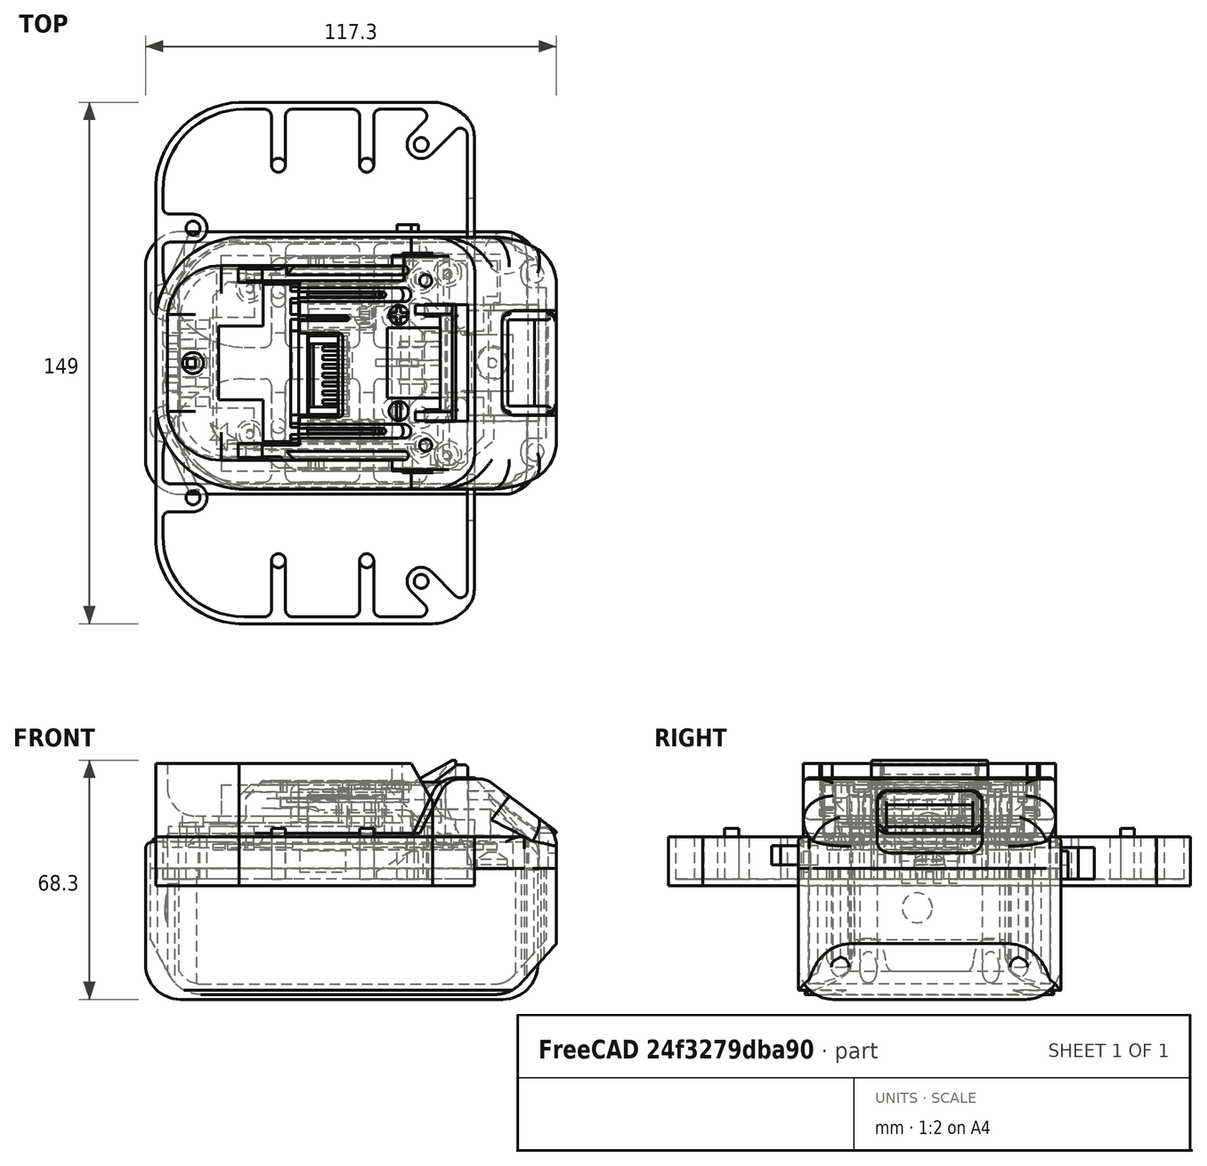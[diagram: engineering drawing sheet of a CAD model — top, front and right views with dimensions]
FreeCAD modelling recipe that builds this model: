
FCSTD DOCUMENT  (FreeCAD 1.0R39319 (Git))
Label: Makita LXT 18V - Battery Adapter v3
License: Creative Commons Attribution 4.0
LicenseURL: https://creativecommons.org/licenses/by/4.0/
objects: Sketcher::SketchObject×28, TechDraw::DrawViewDimension×26, PartDesign::Pocket×18, Part::Feature×12, Image::ImagePlane×8, PartDesign::Pad×6, App::Part×4, PartDesign::Body×4, TechDraw::DrawProjGroupItem×4, PartDesign::Mirrored×3, Mesh::Feature×2, PartDesign::ShapeBinder×2, TechDraw::DrawSVGTemplate×2, TechDraw::DrawPage×2, App::DocumentObjectGroup×1, PartDesign::Fillet×1
note: 204 computed .brp shape members not serialized (recipe doc carries the construction recipe); baked Part::Feature solids carry a one-line shape summary decoded from their .brp

FEATURE [Image::ImagePlane] _d371b5c4eb3955924449baf6266c6d76947dcc9_original  label="7d371b5c4eb3955924449baf6266c6d76947dcc9_original"
  Placement = pos=(41.6,-9,0) rot=(0,0,1;3.14159rad)
  XSize = 126.335
  YSize = 126.335
FEATURE [Part::Feature] Part__Feature  label="Battery Plate"
  shape: bbox 116 x 75.01 x 30.55 mm, 339 faces (baked)
FEATURE [Part::Feature] Part__Feature001  label="Battery Clip"
  shape: bbox 37.48 x 33.31 x 30.03 mm, 74 faces (baked)
FEATURE [Part::Feature] Part__Feature002  label="Yellow Connector"
  shape: bbox 11 x 22.5 x 15.5 mm, 45 faces (baked)
FEATURE [Part::Feature] Part__Feature003  label="Power Clips"
  shape: bbox 20 x 5.5 x 13.5 mm, 10 faces (baked)
FEATURE [Part::Feature] Part__Feature004  label="Power Clips001"
  shape: bbox 18 x 5.5 x 13.5 mm, 10 faces (baked)
FEATURE [Part::Feature] Part__Feature005  label="Power Clips002"
  shape: bbox 20 x 5.5 x 13.5 mm, 10 faces (baked)
FEATURE [App::Part] Power_Clips  label="Power Clips003"
  Group = -> [Part__Feature003,Part__Feature004,Part__Feature005]
  Origin = -> Origin
FEATURE [Part::Feature] Part__Feature006  label="SOLID"
  shape: bbox 81.05 x 58.5 x 1.6 mm, 23 faces (baked)
FEATURE [App::Part] BMS
  Group = -> [Part__Feature002,Power_Clips,Part__Feature006]
  Origin = -> Origin001
FEATURE [Part::Feature] Part__Feature007  label="Case"
  shape: bbox 116 x 75 x 36 mm, 85 faces (baked)
FEATURE [Part::Feature] Part__Feature008  label="Case001"
  shape: bbox 0.6 x 8.5 x 8.5 mm, 3 faces (baked)
FEATURE [App::Part] Case  label="Case002"
  Group = -> [Part__Feature007,Part__Feature008]
  Origin = -> Origin002
FEATURE [App::Part] Battery_LxT_18V_v7  label="Battery LxT 18V v7"
  Group = -> [Part__Feature,Part__Feature001,BMS,Case]
  Origin = -> Origin003
  Placement = pos=(-3.4,0,-1.2) rot=(0,0,1;0rad)
FEATURE [Image::ImagePlane] Makita_Adapter_BL14xx_BL18xx_Zeichnung_v13  label="Makita Adapter BL14xx BL18xx Zeichnung v13"
  Placement = pos=(112.3,-1.5,0) rot=(0,0,1;0rad)
  XSize = 356.175
  YSize = 251.8
FEATURE [Mesh::Feature] Makita18V_BL1860B  label="Makita18V_BL1860B-1.1"
  Placement = pos=(49.6,-1.32e-14,-46.3) rot=(0,0,1;1.5708rad)
FEATURE [Part::Feature] Part__Feature009  label="Makita18V_BL1860B-2.1"
  Placement = pos=(49.7,-1.1e-14,-46.4) rot=(0,0,1;1.5708rad)
  shape: bbox 113.6 x 76.65 x 68.3 mm, 194 faces (baked)
FEATURE [Image::ImagePlane] ScreenShot2021_11_09at3  label="ScreenShot2021-11-09at3"
  Placement = pos=(105.7,-10.5,0) rot=(0,0,1;4.71239rad)
  XSize = 291.833
  YSize = 230.478
FEATURE [Image::ImagePlane] makita_battery_holder_mount  label="makita-battery-holder-mount"
  Placement = pos=(25.3,-0.5,0) rot=(0,0,1;4.71239rad)
  XSize = 296.506
  YSize = 208.851
FEATURE [Sketcher::SketchObject] Sketch  label="Top View"
  ArcFitTolerance = 1e-06
  AttachmentSupport = -> [XY_Plane004]
  FullyConstrained = true
  MakeInternals = false
  MapMode = 5
  sketch-geometry (13):
    g0: ArcOfCircle CenterX=14.9923 CenterY=12.0315 CenterZ=0 NormalX=0 NormalY=0 NormalZ=1 AngleXU=0 Radius=15 StartAngle=1.76483 EndAngle=3.1737
    g1: LineSegment StartX=0 StartY=0 StartZ=0 EndX=0 EndY=11.55 EndZ=0
    g2: LineSegment StartX=12.1 StartY=26.75 StartZ=0 EndX=66.6 EndY=26.75 EndZ=0
    g3: LineSegment StartX=-3.35 StartY=0 StartZ=0 EndX=-3.35 EndY=13 EndZ=0
    g4: LineSegment StartX=-3.35 StartY=0 StartZ=0 EndX=0 EndY=0 EndZ=0
    g5: LineSegment StartX=68.55 StartY=36 StartZ=0 EndX=20.45 EndY=36 EndZ=0
    g6: ArcOfCircle CenterX=21.7106 CenterY=10.8816 CenterZ=0 NormalX=0 NormalY=0 NormalZ=1 AngleXU=0 Radius=25.15 StartAngle=1.62094 EndAngle=3.05726
    g7: LineSegment StartX=87.55 StartY=0 StartZ=0 EndX=87.55 EndY=26.1 EndZ=0
    g8: LineSegment StartX=68.55 StartY=36 StartZ=0 EndX=75.7 EndY=36 EndZ=0
    g9: ArcOfCircle CenterX=79.8506 CenterY=26.1949 CenterZ=0 NormalX=0 NormalY=0 NormalZ=1 AngleXU=0 Radius=7.7 StartAngle=6.27086 EndAngle=6.98074
    g10: ArcOfCircle CenterX=75.3287 CenterY=22.4051 CenterZ=0 NormalX=0 NormalY=0 NormalZ=1 AngleXU=0 Radius=13.6 StartAngle=0.697551 EndAngle=1.54349
    g11: ArcOfCircle CenterX=7.275 CenterY=0 CenterZ=0 NormalX=0 NormalY=0 NormalZ=1 AngleXU=0 Radius=2 StartAngle=0 EndAngle=3.14159
    g12: Circle CenterX=72.4 CenterY=23.9 CenterZ=0 NormalX=0 NormalY=0 NormalZ=1 AngleXU=0 Radius=2
  constraints (44):
    c: PointOnObject(g0,g-2)
    c: Coincident(g1,g-1)
    c: Horizontal(g2)
    c: DistanceY(g1,g1) = 11.55
    c: DistanceY(g0) = 26.75
    c: Coincident(g2,g0)
    c: Coincident(g0,g1)
    c: Radius(g0) = 15
    c: DistanceX(g0) = 12.1
    c: DistanceX(g2) = 66.6
    c: PointOnObject(g3,g-1)
    c: Vertical(g3)
    c: Coincident(g4,g3)
    c: Coincident(g4,g1)
    c: Horizontal(g5)
    c: Coincident(g6,g3)
    c: Coincident(g6,g5)
    c: DistanceX(g3,g-1) = 3.35
    c: DistanceY(g3,g3) = 13
    c: DistanceY(g5) = 36
    c: DistanceX(g5) = 20.45
    c: Radius(g6) = 25.15
    c: DistanceX(g5) = 68.55
    c: PointOnObject(g7,g-1)
    c: Vertical(g7)
    c: DistanceX(g7) = 87.55
    c: DistanceY(g7,g7) = 26.1
    c: Coincident(g8,g5)
    c: Horizontal(g8)
    c: DistanceX(g8,g8) = 7.15
    c: Coincident(g9,g7)
    c: Coincident(g10,g8)
    c: Tangent(g10,g9) = -1.5708
    c: Radius(g10) = 13.6
    c: Radius(g9) = 7.7
    c: DistanceX(g9) = 85.752
    c: PointOnObject(g11,g-1)
    c: PointOnObject(g11,g-1)
    c: Equal(g12,g11)
    c: Diameter(g12) = 4
    c: DistanceX(g11,g7) = 80.275
    c: PointOnObject(g11,g-1)
    c: DistanceX(g12,g7) = 15.15
    c: DistanceY(g12) = 23.9
FEATURE [Part::Feature] Makita18V_BL1860B001  label="Makita18V_BL1860B-2.2"
  shape: bbox 112 x 75 x 68.3 mm, 4064 faces, 0 solids (baked)
FEATURE [Part::Feature] Makita18V_BL1860B002  label="Makita18V_BL1860B-1.2"
  shape: bbox 112 x 75 x 68.3 mm, 4064 faces, 0 solids (baked)
FEATURE [Sketcher::SketchObject] Sketch001  label="Top View001"
  ArcFitTolerance = 1e-06
  AttachmentSupport = -> [XY_Plane005]
  FullyConstrained = true
  MakeInternals = false
  MapMode = 5
  sketch-geometry (11):
    g0: ArcOfCircle CenterX=14.9923 CenterY=12.0315 CenterZ=0 NormalX=0 NormalY=0 NormalZ=1 AngleXU=0 Radius=15 StartAngle=1.76483 EndAngle=3.1737
    g1: LineSegment StartX=0 StartY=0 StartZ=0 EndX=0 EndY=11.55 EndZ=0
    g2: LineSegment StartX=12.1 StartY=26.75 StartZ=0 EndX=66.6 EndY=26.75 EndZ=0
    g3: LineSegment StartX=-3.35 StartY=0 StartZ=0 EndX=-3.35 EndY=13 EndZ=0
    g4: LineSegment StartX=-3.35 StartY=0 StartZ=0 EndX=0 EndY=0 EndZ=0
    g5: LineSegment StartX=68.55 StartY=36 StartZ=0 EndX=20.45 EndY=36 EndZ=0
    g6: ArcOfCircle CenterX=21.7106 CenterY=10.8816 CenterZ=0 NormalX=0 NormalY=0 NormalZ=1 AngleXU=0 Radius=25.15 StartAngle=1.62094 EndAngle=3.05726
    g7: LineSegment StartX=87.55 StartY=0 StartZ=0 EndX=87.55 EndY=26.1 EndZ=0
    g8: LineSegment StartX=68.55 StartY=36 StartZ=0 EndX=75.7 EndY=36 EndZ=0
    g9: ArcOfCircle CenterX=79.8506 CenterY=26.1949 CenterZ=0 NormalX=0 NormalY=0 NormalZ=1 AngleXU=0 Radius=7.7 StartAngle=6.27086 EndAngle=6.98074
    g10: ArcOfCircle CenterX=75.3287 CenterY=22.4051 CenterZ=0 NormalX=0 NormalY=0 NormalZ=1 AngleXU=0 Radius=13.6 StartAngle=0.697551 EndAngle=1.54349
  constraints (36):
    c: PointOnObject(g0,g-2)
    c: Coincident(g1,g-1)
    c: Horizontal(g2)
    c: DistanceY(g1,g1) = 11.55
    c: DistanceY(g0) = 26.75
    c: Coincident(g2,g0)
    c: Coincident(g0,g1)
    c: Radius(g0) = 15
    c: DistanceX(g0) = 12.1
    c: DistanceX(g2) = 66.6
    c: PointOnObject(g3,g-1)
    c: Vertical(g3)
    c: Coincident(g4,g3)
    c: Coincident(g4,g1)
    c: Horizontal(g5)
    c: Coincident(g6,g3)
    c: Coincident(g6,g5)
    c: DistanceX(g3,g-1) = 3.35
    c: DistanceY(g3,g3) = 13
    c: DistanceY(g5) = 36
    c: DistanceX(g5) = 20.45
    c: Radius(g6) = 25.15
    c: DistanceX(g5) = 68.55
    c: PointOnObject(g7,g-1)
    c: Vertical(g7)
    c: DistanceX(g7) = 87.55
    c: DistanceY(g7,g7) = 26.1
    c: Coincident(g8,g5)
    c: Horizontal(g8)
    c: DistanceX(g8,g8) = 7.15
    c: Coincident(g9,g7)
    c: Coincident(g10,g8)
    c: Tangent(g10,g9) = -1.5708
    c: Radius(g10) = 13.6
    c: Radius(g9) = 7.7
    c: DistanceX(g9) = 85.752
FEATURE [Sketcher::SketchObject] Sketch002
  ArcFitTolerance = 1e-06
  AttachmentSupport = -> [XY_Plane005]
  ExternalGeometry = -> [Sketch001]
  FullyConstrained = true
  MakeInternals = false
  MapMode = 5
  sketch-geometry (7):
    g0: LineSegment StartX=87.55 StartY=0 StartZ=0 EndX=87.55 EndY=26.1 EndZ=0
    g1: LineSegment StartX=87.55 StartY=0 StartZ=0 EndX=-3.35 EndY=0 EndZ=0
    g2: LineSegment StartX=-3.35 StartY=0 StartZ=0 EndX=-3.35 EndY=13 EndZ=0
    g3: LineSegment StartX=20.45 StartY=36 StartZ=0 EndX=75.7 EndY=36 EndZ=0
    g4: ArcOfCircle CenterX=21.7106 CenterY=10.8816 CenterZ=0 NormalX=0 NormalY=0 NormalZ=1 AngleXU=0 Radius=25.15 StartAngle=1.62094 EndAngle=3.05726
    g5: ArcOfCircle CenterX=79.8506 CenterY=26.1949 CenterZ=0 NormalX=0 NormalY=0 NormalZ=1 AngleXU=0 Radius=7.7 StartAngle=6.27086 EndAngle=6.98074
    g6: ArcOfCircle CenterX=75.3287 CenterY=22.4051 CenterZ=0 NormalX=0 NormalY=0 NormalZ=1 AngleXU=0 Radius=13.6 StartAngle=0.697551 EndAngle=1.54349
  constraints (19):
    c: PointOnObject(g0,g-1)
    c: Coincident(g0,g-3)
    c: Vertical(g0)
    c: Coincident(g1,g0)
    c: PointOnObject(g1,g-1)
    c: Coincident(g2,g1)
    c: Coincident(g2,g-5)
    c: Vertical(g2)
    c: Coincident(g3,g-5)
    c: Coincident(g3,g-4)
    c: Coincident(g4,g2)
    c: Coincident(g4,g3)
    c: Tangent(g4,g-5)
    c: Coincident(g5,g-4)
    c: Coincident(g5,g0)
    c: Tangent(g5,g-3)
    c: Coincident(g6,g5)
    c: Coincident(g6,g3)
    c: Tangent(g6,g-4)
FEATURE [Sketcher::SketchObject] Sketch003  label="Side View"
  ArcFitTolerance = 1e-06
  AttachmentSupport = -> [XZ_Plane004]
  ExternalGeometry = -> [Sketch]
  FullyConstrained = true
  MakeInternals = false
  MapMode = 5
  Placement = pos=(0,0,0) rot=(1,0,0;1.5708rad)
  sketch-geometry (8):
    g0: LineSegment StartX=69.6 StartY=0 StartZ=0 EndX=75.7032 EndY=13 EndZ=0
    g1: LineSegment StartX=87.55 StartY=17 StartZ=0 EndX=82 EndY=17 EndZ=0
    g2: ArcOfCircle CenterX=82 CenterY=10.0438 CenterZ=0 NormalX=0 NormalY=0 NormalZ=1 AngleXU=0 Radius=6.9562 StartAngle=1.5708 EndAngle=2.70266
    g3: LineSegment StartX=82.15 StartY=17 StartZ=0 EndX=82.15 EndY=22 EndZ=0
    g4: LineSegment StartX=82.15 StartY=22 StartZ=0 EndX=81.15 EndY=22 EndZ=0
    g5: LineSegment StartX=81.15 StartY=22 StartZ=0 EndX=70.65 EndY=16 EndZ=0
    g6: LineSegment StartX=70.65 StartY=16 StartZ=0 EndX=70.65 EndY=15 EndZ=0
    g7: LineSegment StartX=70.65 StartY=15 StartZ=0 EndX=77.1189 EndY=15 EndZ=0
  constraints (26):
    c: PointOnObject(g0,g-1)
    c: Horizontal(g1)
    c: Vertical(g1,g-3)
    c: DistanceX(g0) = 69.6
    c: DistanceY(g0) = 13
    c: DistanceY(g1) = 17
    c: DistanceX(g1) = 82
    c: Tangent(g2,g1) = -1.5708
    c: Tangent(g2,g0) = 1.5708
    c: Radius(g2) = 6.9562
    c: PointOnObject(g3,g1)
    c: Vertical(g3)
    c: Coincident(g3,g4)
    c: Horizontal(g4)
    c: Coincident(g4,g5)
    c: Coincident(g5,g6)
    c: Coincident(g6,g7)
    c: PointOnObject(g7,g2)
    c: Horizontal(g7)
    c: Vertical(g6)
    c: DistanceY(g6) = 15
    c: DistanceX(g6) = 70.65
    c: DistanceY(g6,g6) = 1
    c: DistanceY(g4) = 22
    c: DistanceX(g4) = 81.15
    c: DistanceX(g4,g4) = 1
FEATURE [PartDesign::Body] Body  label="Base Shape"
  AllowCompound = false
  Group = -> [Sketch,Sketch003]
  Origin = -> Origin004
FEATURE [PartDesign::Pad] Pad  label="Shell"
  Direction = (0,0,1)
  Length = 21
  Length2 = 10
  Profile = -> Sketch002
  ReferenceAxis = -> Sketch002 [N_Axis]
  Refine = true
  Suppressed = false
  Type = 0
FEATURE [Sketcher::SketchObject] Sketch004  label="Side View001"
  ArcFitTolerance = 1e-06
  AttachmentSupport = -> [XZ_Plane005]
  ExternalGeometry = -> [Sketch]
  FullyConstrained = true
  MakeInternals = false
  MapMode = 5
  Placement = pos=(0,0,0) rot=(1,0,0;1.5708rad)
  sketch-geometry (8):
    g0: LineSegment StartX=69.6 StartY=0 StartZ=0 EndX=76.8812 EndY=13 EndZ=0
    g1: LineSegment StartX=87.55 StartY=16 StartZ=0 EndX=82 EndY=16 EndZ=0
    g2: ArcOfCircle CenterX=82 CenterY=10.133 CenterZ=0 NormalX=0 NormalY=0 NormalZ=1 AngleXU=0 Radius=5.867 StartAngle=1.5708 EndAngle=2.63103
    g3: LineSegment StartX=82.15 StartY=16 StartZ=0 EndX=82.15 EndY=22 EndZ=0
    g4: LineSegment StartX=82.15 StartY=22 StartZ=0 EndX=81.15 EndY=22 EndZ=0
    g5: LineSegment StartX=81.15 StartY=22 StartZ=0 EndX=70.65 EndY=16 EndZ=0
    g6: LineSegment StartX=70.65 StartY=16 StartZ=0 EndX=70.65 EndY=15 EndZ=0
    g7: LineSegment StartX=70.65 StartY=15 StartZ=0 EndX=78.7237 EndY=15 EndZ=0
  constraints (26):
    c: PointOnObject(g0,g-1)
    c: Horizontal(g1)
    c: Vertical(g1,g-3)
    c: DistanceX(g0) = 69.6
    c: DistanceY(g0) = 13
    c: DistanceY(g1) = 16
    c: DistanceX(g1) = 82
    c: Tangent(g2,g1) = -1.5708
    c: Tangent(g2,g0) = 1.5708
    c: Radius(g2) = 5.867
    c: PointOnObject(g3,g1)
    c: Vertical(g3)
    c: Coincident(g3,g4)
    c: Horizontal(g4)
    c: Coincident(g4,g5)
    c: Coincident(g5,g6)
    c: Coincident(g6,g7)
    c: PointOnObject(g7,g2)
    c: Horizontal(g7)
    c: Vertical(g6)
    c: DistanceY(g6) = 15
    c: DistanceX(g6) = 70.65
    c: DistanceY(g6,g6) = 1
    c: DistanceY(g4) = 22
    c: DistanceX(g4) = 81.15
    c: DistanceX(g4,g4) = 1
FEATURE [Sketcher::SketchObject] Sketch005
  ArcFitTolerance = 1e-06
  AttachmentSupport = -> [Pad]
  ExternalGeometry = -> [Sketch004,Pad]
  FullyConstrained = true
  MakeInternals = false
  MapMode = 5
  Placement = pos=(0,0,0) rot=(1,0,0;1.5708rad)
  sketch-geometry (5):
    g0: LineSegment StartX=69.6 StartY=0 StartZ=0 EndX=76.8812 EndY=13 EndZ=0
    g1: LineSegment StartX=88.55 StartY=16 StartZ=0 EndX=82 EndY=16 EndZ=0
    g2: ArcOfCircle CenterX=82 CenterY=10.133 CenterZ=0 NormalX=0 NormalY=0 NormalZ=1 AngleXU=0 Radius=5.86701 StartAngle=1.5708 EndAngle=2.63103
    g3: LineSegment StartX=88.55 StartY=16 StartZ=0 EndX=88.55 EndY=0 EndZ=0
    g4: LineSegment StartX=88.55 StartY=0 StartZ=0 EndX=69.6 EndY=0 EndZ=0
  constraints (14):
    c: Coincident(g0,g-4)
    c: Horizontal(g1)
    c: Coincident(g1,g-4)
    c: Coincident(g2,g0)
    c: Coincident(g2,g1)
    c: Tangent(g2,g-4)
    c: Coincident(g1,g3)
    c: Vertical(g3)
    c: Coincident(g3,g4)
    c: Coincident(g4,g0)
    c: Horizontal(g4)
    c: Coincident(g0,g-3)
    c: DistanceX(g-5,g1) = 1
    c: DistanceY(g1,g-5) = 5
FEATURE [PartDesign::Pocket] Pocket  label="Side Cutout Pocket"
  BaseFeature = -> Pad
  Direction = (0,1,-2e-16)
  Length = 5
  Length2 = 5
  Profile = -> Sketch005
  ReferenceAxis = -> Sketch005 [N_Axis]
  Refine = true
  Suppressed = false
  Type = 1
FEATURE [Sketcher::SketchObject] Sketch006
  ArcFitTolerance = 1e-06
  AttachmentSupport = -> [Pocket]
  ExternalGeometry = -> [Sketch004]
  FullyConstrained = true
  MakeInternals = false
  MapMode = 5
  Placement = pos=(0,0,0) rot=(1,0,0;1.5708rad)
  sketch-geometry (4):
    g0: LineSegment StartX=82.15 StartY=22 StartZ=0 EndX=81.15 EndY=22 EndZ=0
    g1: LineSegment StartX=68.9 StartY=15 StartZ=0 EndX=82.15 EndY=15 EndZ=0
    g2: LineSegment StartX=82.15 StartY=15 StartZ=0 EndX=82.15 EndY=22 EndZ=0
    g3: LineSegment StartX=68.9 StartY=15 StartZ=0 EndX=81.15 EndY=22 EndZ=0
  constraints (10):
    c: Horizontal(g1)
    c: Coincident(g1,g2)
    c: Coincident(g2,g0)
    c: Vertical(g2)
    c: Coincident(g0,g-3)
    c: PointOnObject(g1,g-4)
    c: Coincident(g3,g1)
    c: Coincident(g3,g0)
    c: Parallel(g3,g-5)
    c: Coincident(g0,g-5)
FEATURE [PartDesign::Pocket] Pocket001  label="Lock Groove Pocket"
  BaseFeature = -> Pocket
  Direction = (0,1,-2e-16)
  Length = 17
  Length2 = 5
  Profile = -> Sketch006
  ReferenceAxis = -> Sketch006 [N_Axis]
  Refine = true
  Suppressed = false
  Type = 0
FEATURE [Sketcher::SketchObject] Sketch007
  ArcFitTolerance = 1e-06
  AttachmentSupport = -> [Pocket001]
  ExternalGeometry = -> [Pocket001]
  FullyConstrained = true
  MakeInternals = false
  MapMode = 5
  Placement = pos=(0,0,0) rot=(1,0,0;3.14159rad)
  sketch-geometry (8):
    g0: ArcOfCircle CenterX=15.3818 CenterY=-12.3502 CenterZ=0 NormalX=0 NormalY=0 NormalZ=1 AngleXU=0 Radius=15.45 StartAngle=3.23557 EndAngle=4.70709
    g1: LineSegment StartX=0 StartY=0 StartZ=0 EndX=78.7237 EndY=0 EndZ=0
    g2: LineSegment StartX=0 StartY=0 StartZ=0 EndX=0 EndY=-13.8 EndZ=0
    g3: LineSegment StartX=15.3 StartY=-27.8 StartZ=0 EndX=66 EndY=-27.8 EndZ=0
    g4: LineSegment StartX=66 StartY=-27.8 StartZ=0 EndX=67 EndY=-28.8 EndZ=0
    g5: LineSegment StartX=78.7237 StartY=-31.35 StartZ=0 EndX=78.7237 EndY=0 EndZ=0
    g6: LineSegment StartX=67 StartY=-28.8 StartZ=0 EndX=67 EndY=-31.35 EndZ=0
    g7: LineSegment StartX=67 StartY=-31.35 StartZ=0 EndX=78.7237 EndY=-31.35 EndZ=0
  constraints (23):
    c: Coincident(g2,g1)
    c: Coincident(g2,g0)
    c: Vertical(g2)
    c: Coincident(g1,g-1)
    c: DistanceY(g2,g2) = 13.8
    c: Radius(g0) = 15.45
    c: Horizontal(g3)
    c: Coincident(g3,g4)
    c: Vertical(g5)
    c: Coincident(g0,g3)
    c: DistanceY(g4,g3) = 1
    c: DistanceY(g0,g-1) = 27.8
    c: DistanceX(g0) = 15.3
    c: DistanceX(g4) = 67
    c: Coincident(g4,g6)
    c: Vertical(g6)
    c: Coincident(g6,g7)
    c: Coincident(g7,g5)
    c: Horizontal(g7)
    c: Angle(g4,g6) = 2.35619
    c: DistanceY(g5,g5) = 31.35
    c: Coincident(g5,g1)
    c: Coincident(g1,g-4)
FEATURE [PartDesign::Pocket] Pocket002  label="Center Pocket"
  BaseFeature = -> Pocket001
  Direction = (0,0,1)
  Length = 15
  Length2 = 5
  Profile = -> Sketch007
  ReferenceAxis = -> Sketch007 [N_Axis]
  Refine = true
  Suppressed = false
  Type = 0
FEATURE [Sketcher::SketchObject] Sketch008
  ArcFitTolerance = 1e-06
  AttachmentSupport = -> [Pocket002]
  ExternalGeometry = -> [Pocket002]
  FullyConstrained = true
  MakeInternals = false
  MapMode = 5
  Placement = pos=(0,27.8,0) rot=(1,0,0;1.5708rad)
  sketch-geometry (9):
    g0: LineSegment StartX=40.3 StartY=6.1 StartZ=0 EndX=40.9 EndY=5.5 EndZ=0
    g1: LineSegment StartX=40.9 StartY=5.5 StartZ=0 EndX=63.1 EndY=5.5 EndZ=0
    g2: LineSegment StartX=63.1 StartY=5.5 StartZ=0 EndX=64.1 EndY=4.5 EndZ=0
    g3: LineSegment StartX=15.3 StartY=6.1 StartZ=0 EndX=40.3 EndY=6.1 EndZ=0
    g4: LineSegment StartX=15.3 StartY=6.1 StartZ=0 EndX=15.3 EndY=15 EndZ=0
    g5: LineSegment StartX=15.3 StartY=15 StartZ=0 EndX=82.15 EndY=15 EndZ=0
    g6: LineSegment StartX=64.1 StartY=4.5 StartZ=0 EndX=64.1 EndY=0 EndZ=0
    g7: LineSegment StartX=64.1 StartY=0 StartZ=0 EndX=82.15 EndY=0 EndZ=0
    g8: LineSegment StartX=82.15 StartY=0 StartZ=0 EndX=82.15 EndY=15 EndZ=0
  constraints (27):
    c: Coincident(g0,g1)
    c: Horizontal(g1)
    c: Coincident(g1,g2)
    c: DistanceY(g1) = 5.5
    c: DistanceX(g1,g2) = 1
    c: Angle(g1,g0) = 2.35619
    c: Coincident(g3,g0)
    c: Horizontal(g3)
    c: Coincident(g3,g4)
    c: Coincident(g4,g5)
    c: Coincident(g2,g6)
    c: PointOnObject(g6,g-1)
    c: Vertical(g6)
    c: Coincident(g6,g7)
    c: PointOnObject(g7,g-1)
    c: Coincident(g7,g8)
    c: Coincident(g8,g5)
    c: Vertical(g8)
    c: Angle(g1,g2) = 2.35619
    c: Horizontal(g5)
    c: Vertical(g4)
    c: DistanceY(g0) = 6.1
    c: Coincident(g4,g-3)
    c: DistanceY(g8,g8) = 15
    c: DistanceX(g3,g3) = 25
    c: Vertical(g5,g-4)
    c: DistanceX(g6,g-5) = 5.5
FEATURE [PartDesign::Pocket] Pocket003  label="Side Ridge Pocket"
  BaseFeature = -> Pocket002
  Direction = (0,1,-2e-16)
  Length = 3
  Length2 = 5
  Profile = -> Sketch008
  ReferenceAxis = -> Sketch008 [N_Axis]
  Refine = true
  Suppressed = false
  Type = 0
FEATURE [Sketcher::SketchObject] Sketch009
  ArcFitTolerance = 1e-06
  AttachmentSupport = -> [Pocket003]
  ExternalGeometry = -> [Pocket003]
  FullyConstrained = true
  MakeInternals = false
  MapMode = 5
  Placement = pos=(0,0,15) rot=(1,0,0;3.14159rad)
  sketch-geometry (10):
    g0: LineSegment StartX=64.05 StartY=0 StartZ=0 EndX=14.55 EndY=0 EndZ=0
    g1: LineSegment StartX=14.55 StartY=0 StartZ=0 EndX=14.55 EndY=-10.5 EndZ=0
    g2: LineSegment StartX=14.55 StartY=-10.5 StartZ=0 EndX=27.25 EndY=-10.5 EndZ=0
    g3: LineSegment StartX=27.25 StartY=-10.5 StartZ=0 EndX=27.25 EndY=-22.5 EndZ=0
    g4: LineSegment StartX=27.25 StartY=-22.5 StartZ=0 EndX=64.05 EndY=-22.5 EndZ=0
    g5: LineSegment StartX=64.05 StartY=-22.5 StartZ=0 EndX=64.05 EndY=0 EndZ=0
    g6: Circle CenterX=72.4 CenterY=-23.9 CenterZ=0 NormalX=0 NormalY=0 NormalZ=1 AngleXU=0 Radius=1.75
    g7: ArcOfCircle CenterX=7.275 CenterY=0 CenterZ=0 NormalX=0 NormalY=0 NormalZ=1 AngleXU=0 Radius=1.75 StartAngle=3.14159 EndAngle=6.28319
    g8: LineSegment StartX=5.525 StartY=2e-16 StartZ=0 EndX=9.025 EndY=-4e-16 EndZ=0
    g9: GeomPoint X=72.4 Y=-30.8 Z=0
  constraints (31):
    c: PointOnObject(g0,g-1)
    c: PointOnObject(g0,g-1)
    c: Coincident(g0,g1)
    c: Vertical(g1)
    c: Coincident(g1,g2)
    c: Horizontal(g2)
    c: Coincident(g2,g3)
    c: Vertical(g3)
    c: Coincident(g3,g4)
    c: Horizontal(g4)
    c: Coincident(g4,g5)
    c: Coincident(g5,g0)
    c: Vertical(g5)
    c: DistanceX(g0,g0) = 49.5
    c: DistanceY(g1,g1) = 10.5
    c: DistanceX(g4,g4) = 36.8
    c: DistanceY(g5,g5) = 22.5
    c: DistanceX(g0,g-3) = 23.5
    c: PointOnObject(g7,g-1)
    c: PointOnObject(g7,g-1)
    c: Coincident(g8,g7)
    c: Coincident(g8,g7)
    c: Equal(g7,g6)
    c: Diameter(g6) = 3.5
    c: Vertical(g6,g-4)
    c: PointOnObject(g9,g-5)
    c: Symmetric(g9,g-4,g6)
    c: Symmetric(g-1,g0,g7)
    c: DistanceX(g7,g-3) = 80.275
    c: DistanceX(g6,g-3) = 15.15
    c: DistanceY(g6,g-3) = 23.9
FEATURE [PartDesign::Pocket] Pocket004  label="Terminal Pocket and Screw Holes"
  BaseFeature = -> Pocket003
  Direction = (0,0,1)
  Length = 5
  Length2 = 5
  Profile = -> Sketch009
  ReferenceAxis = -> Sketch009 [N_Axis]
  Refine = true
  Suppressed = false
  Type = 1
FEATURE [Sketcher::SketchObject] Sketch010
  ArcFitTolerance = 1e-06
  AttachmentSupport = -> [Pocket004]
  ExternalGeometry = -> [Pocket004]
  FullyConstrained = true
  MakeInternals = false
  MapMode = 5
  Placement = pos=(0,0,15) rot=(1,0,0;3.14159rad)
  sketch-geometry (3):
    g0: ArcOfCircle CenterX=7.275 CenterY=0 CenterZ=0 NormalX=0 NormalY=0 NormalZ=1 AngleXU=0 Radius=3 StartAngle=3.14159 EndAngle=6.28319
    g1: LineSegment StartX=4.275 StartY=4e-16 StartZ=0 EndX=10.275 EndY=-7e-16 EndZ=0
    g2: Circle CenterX=72.4 CenterY=-23.9 CenterZ=0 NormalX=0 NormalY=0 NormalZ=1 AngleXU=0 Radius=3
  constraints (8):
    c: PointOnObject(g0,g-1)
    c: PointOnObject(g0,g-1)
    c: Coincident(g1,g0)
    c: Coincident(g1,g0)
    c: Coincident(g0,g-4)
    c: Coincident(g2,g-3)
    c: Equal(g0,g2)
    c: Diameter(g2) = 6
FEATURE [PartDesign::Pocket] Pocket005  label="Screw Head Pockets"
  BaseFeature = -> Pocket004
  Direction = (0,0,1)
  Length = 3
  Length2 = 5
  Profile = -> Sketch010
  ReferenceAxis = -> Sketch010 [N_Axis]
  Refine = true
  Suppressed = false
  Type = 0
FEATURE [Sketcher::SketchObject] Sketch011
  ArcFitTolerance = 1e-06
  AttachmentSupport = -> [Pocket005]
  ExternalGeometry = -> [Pocket005]
  FullyConstrained = true
  MakeInternals = false
  MapMode = 5
  Placement = pos=(0,0,21) rot=(0,0,1;0rad)
  sketch-geometry (8):
    g0: LineSegment StartX=66.55 StartY=0 StartZ=0 EndX=66.55 EndY=12.5 EndZ=0
    g1: LineSegment StartX=66.55 StartY=12.5 StartZ=0 EndX=64.05 EndY=12.5 EndZ=0
    g2: LineSegment StartX=64.05 StartY=12.5 StartZ=0 EndX=64.05 EndY=25 EndZ=0
    g3: LineSegment StartX=64.05 StartY=25 StartZ=0 EndX=24.75 EndY=25 EndZ=0
    g4: LineSegment StartX=24.75 StartY=25 StartZ=0 EndX=24.75 EndY=13 EndZ=0
    g5: LineSegment StartX=24.75 StartY=13 StartZ=0 EndX=12.05 EndY=13 EndZ=0
    g6: LineSegment StartX=12.05 StartY=13 StartZ=0 EndX=12.05 EndY=0 EndZ=0
    g7: LineSegment StartX=12.05 StartY=0 StartZ=0 EndX=66.55 EndY=0 EndZ=0
  constraints (24):
    c: PointOnObject(g0,g-1)
    c: Vertical(g0)
    c: Coincident(g0,g1)
    c: PointOnObject(g1,g-3)
    c: Coincident(g1,g2)
    c: Vertical(g2)
    c: Coincident(g2,g3)
    c: Horizontal(g3)
    c: Coincident(g3,g4)
    c: Vertical(g4)
    c: Coincident(g4,g5)
    c: Horizontal(g5)
    c: Coincident(g5,g6)
    c: PointOnObject(g6,g-1)
    c: Coincident(g6,g7)
    c: Coincident(g7,g0)
    c: Horizontal(g1)
    c: Vertical(g6)
    c: DistanceX(g6,g-5) = 2.5
    c: DistanceX(g-3,g0) = 2.5
    c: DistanceY(g-3,g2) = 2.5
    c: DistanceX(g3,g-4) = 2.5
    c: DistanceY(g-5,g5) = 2.5
    c: DistanceY(g0,g0) = 12.5
FEATURE [PartDesign::Pocket] Pocket006  label="Terminal Ridge Pocket"
  BaseFeature = -> Pocket005
  Direction = (0,0,-1)
  Length = 0
  Length2 = 5
  Offset = 2
  Profile = -> Sketch011
  ReferenceAxis = -> Sketch011 [N_Axis]
  Refine = true
  Suppressed = false
  Type = 3
  UpToFace = -> Pocket005 [Face35]
FEATURE [Mesh::Feature] Makita_LXT____18V___Battery_holder_Battery_Mount_v2  label="Makita LXT  - 18V - Battery holder-Battery Mount v2"
  Placement = pos=(134.5,-83.5,22) rot=(0,1,0;3.14159rad)
FEATURE [Image::ImagePlane] IMG_20260219_225921_416
  XSize = 587.654
  YSize = 814.815
FEATURE [Image::ImagePlane] IMG_20260219_225927_538
  Placement = pos=(53.5,-1.19e-14,0) rot=(0,0,-1;4.71239rad)
  XSize = 81.9006
  YSize = 121.646
FEATURE [Image::ImagePlane] IMG_20260219_225935_189
  XSize = 126.165
  YSize = 82.708
FEATURE [Image::ImagePlane] IMG_20260219_225943_270
  XSize = 72.4776
  YSize = 99.1799
FEATURE [App::DocumentObjectGroup] Group  label="Images"
  Group = -> [_d371b5c4eb3955924449baf6266c6d76947dcc9_original,Makita_Adapter_BL14xx_BL18xx_Zeichnung_v13,ScreenShot2021_11_09at3,makita_battery_holder_mount,IMG_20260219_225921_416,IMG_20260219_225927_538,IMG_20260219_225935_189,IMG_20260219_225943_270]
FEATURE [PartDesign::ShapeBinder] ShapeBinder  label="Top View ShapeBinder"
  Support = -> [Sketch]
  TraceSupport = false
FEATURE [PartDesign::Fillet] Fillet
  Base = -> Pocket006 [Edge72,Edge73]
  BaseFeature = -> Pocket006
  Radius = 8
  Refine = true
  SupportTransform = false
  Suppressed = false
  UseAllEdges = false
FEATURE [PartDesign::Mirrored] Mirrored
  BaseFeature = -> Fillet
  MirrorPlane = -> XZ_Plane005
  Originals = -> [Fillet]
  Refine = true
  Suppressed = false
  TransformMode = 1
FEATURE [PartDesign::Body] Body001  label="Holder"
  AllowCompound = false
  Group = -> [Sketch001,Sketch002,Pad,Sketch004,Sketch005,Pocket,Sketch006,Pocket001,Sketch007,Pocket002,Sketch008,Pocket003,Sketch009,Pocket004,Sketch010,Pocket005,Sketch011,Pocket006,Fillet,Mirrored]
  Origin = -> Origin005
  Placement = pos=(0,2.6e-15,21) rot=(1,0,0;3.14159rad)
  Tip = -> Mirrored
FEATURE [Sketcher::SketchObject] Sketch012
  ArcFitTolerance = 1e-06
  AttachmentSupport = -> [XY_Plane006]
  ExternalGeometry = -> [ShapeBinder]
  FullyConstrained = true
  MakeInternals = false
  MapMode = 5
  sketch-geometry (7):
    g0: LineSegment StartX=-3.35 StartY=13 StartZ=0 EndX=-3.35 EndY=0 EndZ=0
    g1: LineSegment StartX=-3.35 StartY=0 StartZ=0 EndX=87.55 EndY=0 EndZ=0
    g2: LineSegment StartX=87.55 StartY=0 StartZ=0 EndX=87.55 EndY=26.1 EndZ=0
    g3: LineSegment StartX=75.7 StartY=36 StartZ=0 EndX=20.45 EndY=36 EndZ=0
    g4: ArcOfCircle CenterX=21.7106 CenterY=10.8816 CenterZ=0 NormalX=0 NormalY=0 NormalZ=1 AngleXU=0 Radius=25.15 StartAngle=1.62094 EndAngle=3.05726
    g5: ArcOfCircle CenterX=75.3287 CenterY=22.4051 CenterZ=0 NormalX=0 NormalY=0 NormalZ=1 AngleXU=0 Radius=13.6 StartAngle=0.697551 EndAngle=1.54349
    g6: ArcOfCircle CenterX=79.8506 CenterY=26.1949 CenterZ=0 NormalX=0 NormalY=0 NormalZ=1 AngleXU=0 Radius=7.7 StartAngle=6.27086 EndAngle=6.98074
  constraints (19):
    c: Coincident(g0,g-4)
    c: PointOnObject(g0,g-1)
    c: Vertical(g0)
    c: Coincident(g1,g0)
    c: PointOnObject(g1,g-1)
    c: Coincident(g2,g1)
    c: Coincident(g2,g-5)
    c: Vertical(g2)
    c: Coincident(g3,g-3)
    c: Coincident(g3,g-4)
    c: Coincident(g4,g3)
    c: Coincident(g4,g0)
    c: Coincident(g5,g3)
    c: Coincident(g5,g-5)
    c: Coincident(g6,g5)
    c: Coincident(g6,g2)
    c: Equal(g-3,g5)
    c: Equal(g4,g-4)
    c: Equal(g-5,g6)
FEATURE [PartDesign::Pad] Pad001  label="Shell001"
  Direction = (0,0,1)
  Length = 14
  Length2 = 10
  Profile = -> Sketch012
  ReferenceAxis = -> Sketch012 [N_Axis]
  Refine = true
  Reversed = true
  Suppressed = false
  Type = 0
FEATURE [Sketcher::SketchObject] Sketch013
  ArcFitTolerance = 1e-06
  AttachmentSupport = -> [Pad001]
  ExternalGeometry = -> [ShapeBinder]
  FullyConstrained = true
  MakeInternals = false
  MapMode = 5
  sketch-geometry (32):
    g0: Circle CenterX=72.4 CenterY=23.9 CenterZ=0 NormalX=0 NormalY=0 NormalZ=1 AngleXU=0 Radius=2
    g1: ArcOfCircle CenterX=7.275 CenterY=0 CenterZ=0 NormalX=0 NormalY=0 NormalZ=1 AngleXU=0 Radius=4 StartAngle=0 EndAngle=1.5708
    g2: LineSegment StartX=-1.35 StartY=6 StartZ=0 EndX=-1.35 EndY=13 EndZ=0
    g3: LineSegment StartX=69.5716 StartY=26.7284 StartZ=0 EndX=73.4289 EndY=30.5858 EndZ=0
    g4: LineSegment StartX=75.2284 StartY=21.0716 StartZ=0 EndX=82.1358 EndY=27.9789 EndZ=0
    g5: LineSegment StartX=85.55 StartY=0 StartZ=0 EndX=85.55 EndY=26.5647 EndZ=0
    g6: ArcOfCircle CenterX=83.55 CenterY=26.5647 CenterZ=0 NormalX=0 NormalY=0 NormalZ=1 AngleXU=0 Radius=2 StartAngle=6e-16 EndAngle=2.35619
    g7: ArcOfCircle CenterX=72.4 CenterY=23.9 CenterZ=0 NormalX=0 NormalY=0 NormalZ=1 AngleXU=0 Radius=4 StartAngle=2.35619 EndAngle=5.49779
    g8: ArcOfCircle CenterX=72.0147 CenterY=32 CenterZ=0 NormalX=0 NormalY=0 NormalZ=1 AngleXU=0 Radius=2 StartAngle=5.49779 EndAngle=7.85398
    g9: ArcOfCircle CenterX=21.7106 CenterY=10.8816 CenterZ=0 NormalX=0 NormalY=0 NormalZ=1 AngleXU=0 Radius=23.1577 StartAngle=1.62909 EndAngle=3.04999
    g10: ArcOfCircle CenterX=0.65 CenterY=6 CenterZ=0 NormalX=0 NormalY=0 NormalZ=1 AngleXU=0 Radius=2 StartAngle=3.14159 EndAngle=4.71239
    g11: LineSegment StartX=7.275 StartY=4 StartZ=0 EndX=0.65 EndY=4 EndZ=0
    g12: LineSegment StartX=72.0147 StartY=34 StartZ=0 EndX=60.8647 EndY=34 EndZ=0
    g13: LineSegment StartX=58.8647 StartY=32 StartZ=0 EndX=58.8647 EndY=18 EndZ=0
    g14: LineSegment StartX=54.8647 StartY=18 StartZ=0 EndX=54.8647 EndY=32 EndZ=0
    g15: LineSegment StartX=33.6615 StartY=32 StartZ=0 EndX=33.6615 EndY=18 EndZ=0
    g16: LineSegment StartX=29.6615 StartY=18 StartZ=0 EndX=29.6615 EndY=32 EndZ=0
    g17: LineSegment StartX=20.3615 StartY=34 StartZ=0 EndX=27.6615 EndY=34 EndZ=0
    g18: ArcOfCircle CenterX=27.6615 CenterY=32 CenterZ=0 NormalX=0 NormalY=0 NormalZ=1 AngleXU=0 Radius=2 StartAngle=6e-16 EndAngle=1.5708
    g19: ArcOfCircle CenterX=35.6615 CenterY=32 CenterZ=0 NormalX=0 NormalY=0 NormalZ=1 AngleXU=0 Radius=2 StartAngle=1.5708 EndAngle=3.14159
    g20: ArcOfCircle CenterX=52.8647 CenterY=32 CenterZ=0 NormalX=0 NormalY=0 NormalZ=1 AngleXU=0 Radius=2 StartAngle=0 EndAngle=1.5708
    g21: ArcOfCircle CenterX=60.8647 CenterY=32 CenterZ=0 NormalX=0 NormalY=0 NormalZ=1 AngleXU=0 Radius=2 StartAngle=1.5708 EndAngle=3.14159
    g22: ArcOfCircle CenterX=56.8647 CenterY=18 CenterZ=0 NormalX=0 NormalY=0 NormalZ=1 AngleXU=0 Radius=2 StartAngle=3.14159 EndAngle=6.28319
    g23: ArcOfCircle CenterX=31.6615 CenterY=18 CenterZ=0 NormalX=0 NormalY=0 NormalZ=1 AngleXU=0 Radius=2 StartAngle=3.14159 EndAngle=6.28319
    g24: LineSegment StartX=35.6615 StartY=34 StartZ=0 EndX=52.8647 EndY=34 EndZ=0
    g25: LineSegment StartX=59.55 StartY=0 StartZ=0 EndX=59.55 EndY=1 EndZ=0
    g26: LineSegment StartX=59.55 StartY=1 StartZ=0 EndX=71.55 EndY=1 EndZ=0
    g27: LineSegment StartX=71.55 StartY=1 StartZ=0 EndX=71.55 EndY=0 EndZ=0
    g28: LineSegment StartX=71.55 StartY=0 StartZ=0 EndX=85.55 EndY=0 EndZ=0
    g29: LineSegment StartX=59.55 StartY=0 StartZ=0 EndX=11.275 EndY=0 EndZ=0
    g30: ArcOfCircle CenterX=7.275 CenterY=0 CenterZ=0 NormalX=0 NormalY=0 NormalZ=1 AngleXU=0 Radius=2 StartAngle=0 EndAngle=3.14159
    g31: LineSegment StartX=9.275 StartY=0 StartZ=0 EndX=5.275 EndY=2e-16 EndZ=0
  constraints (84):
    c: PointOnObject(g5,g-1)
    c: Coincident(g0,g-6)
    c: Diameter(g0) = 4
    c: Vertical(g2)
    c: Vertical(g5)
    c: Coincident(g9,g2)
    c: Horizontal(g11)
    c: Tangent(g11,g10) = 1.5708
    c: Tangent(g7,g3) = 1.5708
    c: Tangent(g7,g4) = -1.5708
    c: Tangent(g6,g4) = 1.5708
    c: Tangent(g6,g5) = -1.5708
    c: Tangent(g8,g3) = -1.5708
    c: Parallel(g3,g4)
    c: Equal(g1,g7)
    c: Coincident(g7,g0)
    c: Diameter(g7) = 8
    c: Angle(g4,g5) = 0.785398
    c: Equal(g10,g8)
    c: Equal(g8,g6)
    c: Horizontal(g12)
    c: Vertical(g13)
    c: Vertical(g14)
    c: Vertical(g16)
    c: Vertical(g15)
    c: Equal(g13,g14)
    c: Equal(g14,g15)
    c: Equal(g15,g16)
    c: Coincident(g17,g9)
    c: Horizontal(g17)
    c: Horizontal(g24)
    c: Horizontal(g20,g12)
    c: Horizontal(g12,g17)
    c: Coincident(g-5,g9)
    c: Horizontal(g-5,g2)
    c: DistanceX(g-5,g2) = 2
    c: Tangent(g10,g2) = 1.5708
    c: Tangent(g18,g17) = 1.5708
    c: Tangent(g18,g16) = -1.5708
    c: Tangent(g23,g16) = 1.5708
    c: Tangent(g23,g15) = 1.5708
    c: Tangent(g19,g15) = -1.5708
    c: Tangent(g24,g19) = 1.5708
    c: Tangent(g24,g20) = 1.5708
    c: Tangent(g20,g14) = -1.5708
    c: Tangent(g22,g14) = 1.5708
    c: Tangent(g22,g13) = 1.5708
    c: Tangent(g21,g13) = -1.5708
    c: Tangent(g21,g12) = -1.5708
    c: Tangent(g12,g8) = -1.5708
    c: Equal(g8,g21)
    c: Equal(g20,g19)
    c: Radius(g10) = 2
    c: Equal(g22,g23)
    c: DistanceX(g16,g15) = 4
    c: DistanceY(g9,g-5) = 2
    c: DistanceX(g17,g17) = 7.3
    c: DistanceX(g12,g12) = 11.15
    c: DistanceY(g14,g20) = 16
    c: DistanceX(g5,g-8) = 2
    c: Tangent(g11,g1) = -1.5708
    c: PointOnObject(g25,g-1)
    c: Vertical(g25)
    c: Coincident(g25,g26)
    c: Horizontal(g26)
    c: Coincident(g26,g27)
    c: PointOnObject(g27,g-1)
    c: Vertical(g27)
    c: Coincident(g27,g28)
    c: Coincident(g28,g5)
    c: DistanceY(g25,g25) = 1  'TabWidth'
    c: DistanceX(g27,g-8) = 16
    c: DistanceX(g26,g26) = 12  'TabLength'
    c: Coincident(g29,g25)
    c: Coincident(g29,g1)
    c: Horizontal(g29)
    c: Coincident(g1,g-7)
    c: Coincident(g30,g1)
    c: PointOnObject(g30,g-1)
    c: PointOnObject(g30,g-1)
    c: Coincident(g31,g30)
    c: Coincident(g31,g30)
    c: Equal(g30,g0)
    c: Diameter(g30) = 4
FEATURE [PartDesign::Pocket] Pocket007
  BaseFeature = -> Pad001
  Direction = (0,0,-1)
  Length = 0
  Length2 = 5
  Offset = -2
  Profile = -> Sketch013
  ReferenceAxis = -> Sketch013 [N_Axis]
  Refine = true
  Suppressed = false
  Type = 3
  UpToFace = -> Pad001 [Face9]
FEATURE [Sketcher::SketchObject] Sketch014
  ArcFitTolerance = 1e-06
  AttachmentSupport = -> [Pocket007]
  ExternalGeometry = -> [Pocket007]
  FullyConstrained = true
  MakeInternals = false
  MapMode = 5
  Placement = pos=(0,0,0) rot=(1,0,0;1.5708rad)
  sketch-geometry (5):
    g0: LineSegment StartX=59.55 StartY=0 StartZ=0 EndX=59.55 EndY=-10 EndZ=0
    g1: LineSegment StartX=59.55 StartY=-10 StartZ=0 EndX=69.55 EndY=-4 EndZ=0
    g2: LineSegment StartX=71.55 StartY=0 StartZ=0 EndX=59.55 EndY=0 EndZ=0
    g3: LineSegment StartX=71.55 StartY=0 StartZ=0 EndX=71.55 EndY=-4 EndZ=0
    g4: LineSegment StartX=71.55 StartY=-4 StartZ=0 EndX=69.55 EndY=-4 EndZ=0
  constraints (13):
    c: Coincident(g-3,g0)
    c: Vertical(g0)
    c: Coincident(g0,g1)
    c: Coincident(g2,g0)
    c: Coincident(g2,g3)
    c: Coincident(g3,g4)
    c: Coincident(g4,g1)
    c: Horizontal(g4)
    c: Vertical(g3)
    c: Coincident(g2,g-3)
    c: DistanceY(g-4,g3) = 8
    c: DistanceX(g4,g4) = 2
    c: DistanceY(g-4,g0) = 2
FEATURE [PartDesign::Pocket] Pocket008
  BaseFeature = -> Pocket007
  Direction = (0,1,-2e-16)
  Length = 5
  Length2 = 5
  Profile = -> Sketch014
  ReferenceAxis = -> Sketch014 [N_Axis]
  Refine = true
  Suppressed = false
  Type = 2
FEATURE [Sketcher::SketchObject] Sketch015
  ArcFitTolerance = 1e-06
  AttachmentSupport = -> [Pocket008]
  ExternalGeometry = -> [Pocket008]
  FullyConstrained = true
  MakeInternals = false
  MapMode = 5
  Placement = pos=(87.55,0,0) rot=(0.57735,0.57735,0.57735;2.0944rad)
  sketch-geometry (4):
    g0: LineSegment StartX=0 StartY=-3 StartZ=0 EndX=0 EndY=-12 EndZ=0
    g1: LineSegment StartX=0 StartY=-12 StartZ=0 EndX=8.5 EndY=-12 EndZ=0
    g2: LineSegment StartX=8.5 StartY=-12 StartZ=0 EndX=8.5 EndY=-3 EndZ=0
    g3: LineSegment StartX=8.5 StartY=-3 StartZ=0 EndX=0 EndY=-3 EndZ=0
  constraints (12):
    c: Coincident(g0,g1)
    c: Coincident(g1,g2)
    c: Coincident(g2,g3)
    c: Coincident(g3,g0)
    c: Vertical(g0)
    c: Vertical(g2)
    c: Horizontal(g1)
    c: Horizontal(g3)
    c: DistanceY(g2,g2) = 9
    c: Coincident(g0,g-3)
    c: DistanceX(g1,g1) = 8.5
    c: DistanceY(g0,g-1) = 3
FEATURE [PartDesign::Pocket] Pocket009
  BaseFeature = -> Pocket008
  Direction = (-1,0,0)
  Length = 5
  Length2 = 5
  Profile = -> Sketch015
  ReferenceAxis = -> Sketch015 [N_Axis]
  Refine = true
  Suppressed = false
  Type = 2
FEATURE [Sketcher::SketchObject] Sketch016
  ArcFitTolerance = 1e-06
  AttachmentSupport = -> [Pocket009]
  ExternalGeometry = -> [Pocket009]
  FullyConstrained = true
  MakeInternals = false
  MapMode = 5
  sketch-geometry (2):
    g0: Circle CenterX=56.8647 CenterY=18 CenterZ=0 NormalX=0 NormalY=0 NormalZ=1 AngleXU=0 Radius=2
    g1: Circle CenterX=31.6615 CenterY=18 CenterZ=0 NormalX=0 NormalY=0 NormalZ=1 AngleXU=0 Radius=2
  constraints (4):
    c: Coincident(g0,g-3)
    c: PointOnObject(g-3,g0)
    c: Coincident(g1,g-4)
    c: PointOnObject(g-4,g1)
FEATURE [PartDesign::Pad] Pad002
  BaseFeature = -> Pocket009
  Direction = (0,0,1)
  Length = 2.5
  Length2 = 10
  Profile = -> Sketch016
  ReferenceAxis = -> Sketch016 [N_Axis]
  Refine = true
  Suppressed = false
  Type = 0
FEATURE [PartDesign::Mirrored] Mirrored001  label="No USB"
  BaseFeature = -> Pad002
  MirrorPlane = -> XZ_Plane006
  Originals = -> [Pad002]
  Refine = true
  Suppressed = false
  TransformMode = 1
FEATURE [Sketcher::SketchObject] Sketch017
  ArcFitTolerance = 1e-06
  AttachmentSupport = -> [Mirrored001]
  ExternalGeometry = -> [Mirrored001]
  FullyConstrained = true
  MakeInternals = false
  MapMode = 5
  Placement = pos=(-5.08e-14,-36,-1.6e-14) rot=(1,0,0;1.5708rad)
  sketch-geometry (7):
    g0: LineSegment StartX=37.6631 StartY=-4 StartZ=0 EndX=37.6631 EndY=-10 EndZ=0
    g1: LineSegment StartX=37.6631 StartY=-10 StartZ=0 EndX=50.8631 EndY=-10 EndZ=0
    g2: LineSegment StartX=50.8631 StartY=-10 StartZ=0 EndX=50.8631 EndY=-4 EndZ=0
    g3: LineSegment StartX=50.8631 StartY=-4 StartZ=0 EndX=37.6631 EndY=-4 EndZ=0
    g4: GeomPoint [constr] X=44.2631 Y=-7 Z=0
    g5: GeomPoint X=52.8647 Y=-7 Z=0
    g6: GeomPoint X=35.6615 Y=-7 Z=0
  constraints (16):
    c: Coincident(g0,g1)
    c: Coincident(g1,g2)
    c: Coincident(g2,g3)
    c: Coincident(g3,g0)
    c: Vertical(g0)
    c: Vertical(g2)
    c: Horizontal(g1)
    c: Horizontal(g3)
    c: Symmetric(g2,g0,g4)
    c: PointOnObject(g5,g-3)
    c: PointOnObject(g6,g-4)
    c: Horizontal(g5,g6)
    c: Symmetric(g5,g6,g4)
    c: DistanceX(g1,g1) = 13.2
    c: DistanceY(g0,g0) = 6
    c: DistanceY(g-4,g0) = 2
FEATURE [PartDesign::Pocket] Pocket010  label="USB Pocket"
  BaseFeature = -> Mirrored001
  Direction = (1.4e-15,1,-2e-16)
  Length = 5
  Length2 = 5
  Profile = -> Sketch017
  ReferenceAxis = -> Sketch017 [N_Axis]
  Refine = true
  Suppressed = false
  Type = 2
FEATURE [PartDesign::Body] Body002  label="Single Bottom"
  AllowCompound = false
  Group = -> [ShapeBinder,Sketch012,Pad001,Sketch013,Pocket007,Sketch014,Pocket008,Sketch015,Pocket009,Sketch016,Pad002,Mirrored001,Sketch017,Pocket010]
  Origin = -> Origin006
  Tip = -> Pocket010
FEATURE [PartDesign::ShapeBinder] ShapeBinder001
  Support = -> [Sketch]
  TraceSupport = false
FEATURE [Sketcher::SketchObject] Sketch018
  ArcFitTolerance = 1e-06
  AttachmentSupport = -> [XY_Plane007]
  ExternalGeometry = -> [ShapeBinder001]
  FullyConstrained = true
  MakeInternals = false
  MapMode = 5
  sketch-geometry (9):
    g0: LineSegment StartX=75.7 StartY=74.5 StartZ=0 EndX=20.45 EndY=74.5 EndZ=0
    g1: ArcOfCircle CenterX=21.7106 CenterY=49.3816 CenterZ=0 NormalX=0 NormalY=0 NormalZ=1 AngleXU=0 Radius=25.15 StartAngle=1.62094 EndAngle=3.05726
    g2: ArcOfCircle CenterX=75.3287 CenterY=60.9051 CenterZ=0 NormalX=0 NormalY=0 NormalZ=1 AngleXU=0 Radius=13.6 StartAngle=0.697551 EndAngle=1.54349
    g3: ArcOfCircle CenterX=79.8506 CenterY=64.6949 CenterZ=0 NormalX=0 NormalY=0 NormalZ=1 AngleXU=0 Radius=7.7 StartAngle=0.0123238 EndAngle=0.697551
    g4: LineSegment StartX=-3.35 StartY=51.5 StartZ=0 EndX=-3.35 EndY=38.5 EndZ=0
    g5: LineSegment StartX=87.55 StartY=38.5 StartZ=0 EndX=87.55 EndY=64.7898 EndZ=0
    g6: LineSegment StartX=87.55 StartY=38.5 StartZ=0 EndX=87.55 EndY=0 EndZ=0
    g7: LineSegment StartX=87.55 StartY=0 StartZ=0 EndX=-3.35 EndY=0 EndZ=0
    g8: LineSegment StartX=-3.35 StartY=0 StartZ=0 EndX=-3.35 EndY=38.5 EndZ=0
  constraints (30):
    c: Horizontal(g0)
    c: Coincident(g1,g0)
    c: Coincident(g2,g0)
    c: Tangent(g3,g2) = -1.5708
    c: Equal(g-4,g2)
    c: Equal(g-3,g3)
    c: Vertical(g-5,g0)
    c: Vertical(g-4,g2)
    c: Vertical(g-4,g0)
    c: Vertical(g1,g-5)
    c: Vertical(g-3,g3)
    c: Coincident(g4,g1)
    c: Vertical(g4)
    c: Coincident(g5,g3)
    c: Vertical(g5)
    c: Vertical(g5,g-3)
    c: Vertical(g4,g-5)
    c: Equal(g-8,g4)
    c: DistanceY(g-5) = 36
    c: DistanceY(g0) = 74.5
    c: DistanceY(g-3) = 26.1949
    c: DistanceY(g5,g3) = 26.1949
    c: Horizontal(g4,g5)
    c: Coincident(g5,g6)
    c: Coincident(g6,g7)
    c: Coincident(g7,g-8)
    c: Coincident(g7,g8)
    c: Coincident(g8,g4)
    c: Horizontal(g7)
    c: Vertical(g6)
FEATURE [PartDesign::Pad] Pad003
  Direction = (0,0,1)
  Length = 14
  Length2 = 10
  Profile = -> Sketch018
  ReferenceAxis = -> Sketch018 [N_Axis]
  Refine = true
  Reversed = true
  Suppressed = false
  Type = 0
FEATURE [Sketcher::SketchObject] Sketch019
  ArcFitTolerance = 1e-06
  AttachmentSupport = -> [Pad003]
  ExternalGeometry = -> [Pad003,ShapeBinder001]
  FullyConstrained = false
  MakeInternals = false
  MapMode = 5
  sketch-geometry (56):
    g0: Circle CenterX=72.4 CenterY=62.4 CenterZ=0 NormalX=0 NormalY=0 NormalZ=1 AngleXU=0 Radius=2
    g1: ArcOfCircle CenterX=7.275 CenterY=38.5 CenterZ=0 NormalX=0 NormalY=0 NormalZ=1 AngleXU=0 Radius=4 StartAngle=0 EndAngle=1.5708
    g2: ArcOfCircle CenterX=72.4 CenterY=62.4 CenterZ=0 NormalX=0 NormalY=0 NormalZ=1 AngleXU=0 Radius=4 StartAngle=2.35619 EndAngle=5.49779
    g3: ArcOfCircle CenterX=31.66 CenterY=56.5 CenterZ=0 NormalX=0 NormalY=0 NormalZ=1 AngleXU=0 Radius=2 StartAngle=3.14159 EndAngle=6.28319
    g4: ArcOfCircle CenterX=56.86 CenterY=56.5 CenterZ=0 NormalX=0 NormalY=0 NormalZ=1 AngleXU=0 Radius=2 StartAngle=3.14159 EndAngle=6.28319
    g5: LineSegment StartX=69.5716 StartY=65.2284 StartZ=0 EndX=73.4289 EndY=69.0858 EndZ=0
    g6: LineSegment StartX=75.2284 StartY=59.5716 StartZ=0 EndX=82.1358 EndY=66.4789 EndZ=0
    g7: ArcOfCircle CenterX=7.275 CenterY=38.5 CenterZ=0 NormalX=0 NormalY=0 NormalZ=1 AngleXU=0 Radius=2 StartAngle=-9e-16 EndAngle=3.14159
    g8: LineSegment StartX=7.275 StartY=42.5 StartZ=0 EndX=0.65 EndY=42.5 EndZ=0
    g9: LineSegment StartX=-1.35 StartY=44.5 StartZ=0 EndX=-1.35 EndY=49.2 EndZ=0
    g10: LineSegment StartX=85.55 StartY=65.0647 StartZ=0 EndX=85.55 EndY=38.5 EndZ=0
    g11: LineSegment [constr] StartX=85.55 StartY=38.5 StartZ=0 EndX=11.275 EndY=38.5 EndZ=0
    g12: LineSegment StartX=9.275 StartY=38.5 StartZ=0 EndX=5.275 EndY=38.5 EndZ=0
    g13: ArcOfCircle CenterX=21.95 CenterY=49.2 CenterZ=0 NormalX=0 NormalY=0 NormalZ=1 AngleXU=0 Radius=23.3 StartAngle=1.5708 EndAngle=3.14159
    g14: ArcOfCircle CenterX=72.0147 CenterY=70.5 CenterZ=0 NormalX=0 NormalY=0 NormalZ=1 AngleXU=0 Radius=2 StartAngle=5.49779 EndAngle=7.85398
    g15: ArcOfCircle CenterX=83.55 CenterY=65.0647 CenterZ=0 NormalX=0 NormalY=0 NormalZ=1 AngleXU=0 Radius=2 StartAngle=-2.7e-15 EndAngle=2.35619
    g16: ArcOfCircle CenterX=0.65 CenterY=44.5 CenterZ=0 NormalX=0 NormalY=0 NormalZ=1 AngleXU=0 Radius=2 StartAngle=3.14159 EndAngle=4.71239
    g17: LineSegment StartX=21.95 StartY=72.5 StartZ=0 EndX=27.66 EndY=72.5 EndZ=0
    g18: LineSegment StartX=35.66 StartY=72.5 StartZ=0 EndX=52.86 EndY=72.5 EndZ=0
    g19: LineSegment StartX=60.86 StartY=72.5 StartZ=0 EndX=72.0147 EndY=72.5 EndZ=0
    g20: ArcOfCircle CenterX=27.66 CenterY=70.5 CenterZ=0 NormalX=0 NormalY=0 NormalZ=1 AngleXU=0 Radius=2 StartAngle=2.7e-15 EndAngle=1.5708
    g21: ArcOfCircle CenterX=35.66 CenterY=70.5 CenterZ=0 NormalX=0 NormalY=0 NormalZ=1 AngleXU=0 Radius=2 StartAngle=1.5708 EndAngle=3.14159
    g22: ArcOfCircle CenterX=52.86 CenterY=70.5 CenterZ=0 NormalX=0 NormalY=0 NormalZ=1 AngleXU=0 Radius=2 StartAngle=1.7e-15 EndAngle=1.5708
    g23: ArcOfCircle CenterX=60.86 CenterY=70.5 CenterZ=0 NormalX=0 NormalY=0 NormalZ=1 AngleXU=0 Radius=2 StartAngle=1.5708 EndAngle=3.14159
    g24: LineSegment StartX=58.86 StartY=56.5 StartZ=0 EndX=58.86 EndY=70.5 EndZ=0
    g25: LineSegment StartX=54.86 StartY=56.5 StartZ=0 EndX=54.86 EndY=70.5 EndZ=0
    g26: LineSegment StartX=33.66 StartY=70.5 StartZ=0 EndX=33.66 EndY=56.5 EndZ=0
    g27: LineSegment StartX=29.66 StartY=56.5 StartZ=0 EndX=29.66 EndY=70.5 EndZ=0
    g28: Circle CenterX=72.4 CenterY=14.6 CenterZ=0 NormalX=0 NormalY=0 NormalZ=1 AngleXU=0 Radius=2
    g29: ArcOfCircle CenterX=7.275 CenterY=38.5 CenterZ=0 NormalX=0 NormalY=0 NormalZ=1 AngleXU=0 Radius=4 StartAngle=4.71239 EndAngle=6.28319
    g30: ArcOfCircle CenterX=72.4 CenterY=14.6 CenterZ=0 NormalX=0 NormalY=0 NormalZ=1 AngleXU=0 Radius=4 StartAngle=0.785398 EndAngle=3.92699
    g31: ArcOfCircle CenterX=31.66 CenterY=20.5 CenterZ=0 NormalX=0 NormalY=0 NormalZ=1 AngleXU=0 Radius=2 StartAngle=0 EndAngle=3.14159
    g32: ArcOfCircle CenterX=56.86 CenterY=20.5 CenterZ=0 NormalX=0 NormalY=0 NormalZ=1 AngleXU=0 Radius=2 StartAngle=0 EndAngle=3.14159
    g33: LineSegment StartX=69.5716 StartY=11.7716 StartZ=0 EndX=73.4289 EndY=7.91421 EndZ=0
    g34: LineSegment StartX=75.2284 StartY=17.4284 StartZ=0 EndX=82.1358 EndY=10.5211 EndZ=0
    g35: ArcOfCircle CenterX=7.275 CenterY=38.5 CenterZ=0 NormalX=0 NormalY=0 NormalZ=1 AngleXU=0 Radius=2 StartAngle=3.14159 EndAngle=6.28319
    g36: LineSegment StartX=7.275 StartY=34.5 StartZ=0 EndX=0.65 EndY=34.5 EndZ=0
    g37: LineSegment StartX=-1.35 StartY=32.5 StartZ=0 EndX=-1.35 EndY=27.8 EndZ=0
    g38: LineSegment StartX=85.55 StartY=11.9353 StartZ=0 EndX=85.55 EndY=38.5 EndZ=0
    g39: LineSegment [constr] StartX=85.55 StartY=38.5 StartZ=0 EndX=11.275 EndY=38.5 EndZ=0
    g40: LineSegment StartX=9.275 StartY=38.5 StartZ=0 EndX=5.275 EndY=38.5 EndZ=0
    g41: ArcOfCircle CenterX=21.95 CenterY=27.8 CenterZ=0 NormalX=0 NormalY=0 NormalZ=1 AngleXU=0 Radius=23.3 StartAngle=3.14159 EndAngle=4.71239
    g42: ArcOfCircle CenterX=72.0147 CenterY=6.5 CenterZ=0 NormalX=0 NormalY=0 NormalZ=1 AngleXU=0 Radius=2 StartAngle=4.71239 EndAngle=7.06858
    g43: ArcOfCircle CenterX=83.55 CenterY=11.9353 CenterZ=0 NormalX=0 NormalY=0 NormalZ=1 AngleXU=0 Radius=2 StartAngle=3.92699 EndAngle=6.28319
    g44: ArcOfCircle CenterX=0.65 CenterY=32.5 CenterZ=0 NormalX=0 NormalY=0 NormalZ=1 AngleXU=0 Radius=2 StartAngle=1.5708 EndAngle=3.14159
    g45: LineSegment StartX=21.95 StartY=4.5 StartZ=0 EndX=27.66 EndY=4.5 EndZ=0
    g46: LineSegment StartX=35.66 StartY=4.5 StartZ=0 EndX=52.86 EndY=4.5 EndZ=0
    g47: LineSegment StartX=60.86 StartY=4.5 StartZ=0 EndX=72.0147 EndY=4.5 EndZ=0
    g48: ArcOfCircle CenterX=27.66 CenterY=6.5 CenterZ=0 NormalX=0 NormalY=0 NormalZ=1 AngleXU=0 Radius=2 StartAngle=4.71239 EndAngle=6.28319
    g49: ArcOfCircle CenterX=35.66 CenterY=6.5 CenterZ=0 NormalX=0 NormalY=0 NormalZ=1 AngleXU=0 Radius=2 StartAngle=3.14159 EndAngle=4.71239
    g50: ArcOfCircle CenterX=52.86 CenterY=6.5 CenterZ=0 NormalX=0 NormalY=0 NormalZ=1 AngleXU=0 Radius=2 StartAngle=4.71239 EndAngle=6.28319
    g51: ArcOfCircle CenterX=60.86 CenterY=6.5 CenterZ=0 NormalX=0 NormalY=0 NormalZ=1 AngleXU=0 Radius=2 StartAngle=3.14159 EndAngle=4.71239
    g52: LineSegment StartX=58.86 StartY=20.5 StartZ=0 EndX=58.86 EndY=6.5 EndZ=0
    g53: LineSegment StartX=54.86 StartY=20.5 StartZ=0 EndX=54.86 EndY=6.5 EndZ=0
    g54: LineSegment StartX=33.66 StartY=6.5 StartZ=0 EndX=33.66 EndY=20.5 EndZ=0
    g55: LineSegment StartX=29.66 StartY=20.5 StartZ=0 EndX=29.66 EndY=6.5 EndZ=0
  constraints (126):
    c: DistanceY(g0,g-4) = 12.1
    c: Coincident(g2,g0)
    c: Equal(g3,g4)
    c: Horizontal(g4,g3)
    c: Coincident(g7,g1)
    c: Vertical(g10)
    c: Coincident(g11,g10)
    c: Coincident(g11,g1)
    c: Horizontal(g11)
    c: Horizontal(g1,g1)
    c: Vertical(g1,g-7)
    c: Coincident(g12,g7)
    c: Coincident(g12,g7)
    c: Horizontal(g1,g7)
    c: Horizontal(g1,g7)
    c: Vertical(g9)
    c: Tangent(g8,g1) = -1.5708
    c: Tangent(g16,g8) = 1.5708
    c: Tangent(g16,g9) = 1.5708
    c: Tangent(g15,g10) = 1.5708
    c: Tangent(g15,g6) = 1.5708
    c: Tangent(g6,g2) = -1.5708
    c: Tangent(g5,g2) = 1.5708
    c: Tangent(g14,g5) = -1.5708
    c: Angle(g6,g10) = 0.785398
    c: Parallel(g5,g6)
    c: DistanceX(g10,g-5) = 2
    c: DistanceX(g-3,g9) = 2
    c: DistanceY(g13,g-3) = 2
    c: Equal(g2,g1)
    c: Radius(g2) = 4
    c: Vertical(g-6,g0)
    c: Horizontal(g8)
    c: Equal(g16,g14)
    c: Equal(g14,g15)
    c: Radius(g14) = 2
    c: DistanceY(g1,g0) = 23.9
    c: Tangent(g13,g9) = 1.5708
    c: Horizontal(g17)
    c: Horizontal(g18)
    c: Tangent(g19,g14) = 1.5708
    c: Horizontal(g19)
    c: Horizontal(g19,g18)
    c: Horizontal(g18,g17)
    c: Tangent(g17,g13) = 1.5708
    c: Vertical(g26)
    c: Tangent(g20,g17) = 1.5708
    c: Tangent(g27,g20) = -1.5708
    c: Tangent(g27,g3) = 1.5708
    c: Tangent(g26,g3) = 1.5708
    c: Tangent(g26,g21) = -1.5708
    c: Tangent(g21,g18) = 1.5708
    c: Tangent(g22,g18) = 1.5708
    c: Tangent(g25,g22) = -1.5708
    c: Tangent(g25,g4) = 1.5708
    c: Tangent(g24,g4) = -1.5708
    c: Tangent(g24,g23) = 1.5708
    c: Tangent(g23,g19) = 1.5708
    c: Vertical(g24)
    c: Vertical(g25)
    c: Vertical(g27)
    c: Equal(g14,g23)
    c: Equal(g23,g22)
    c: Equal(g22,g21)
    c: Equal(g21,g20)
    c: Equal(g4,g21)
    c: DistanceX(g4,g0) = 15.54
    c: DistanceX(g3,g4) = 25.2
    c: DistanceY(g1,g3) = 18
    c: DistanceX(g-3,g13) = 1.5
    c: Coincident(g30,g28)
    c: Equal(g31,g32)
    c: Coincident(g35,g29)
    c: Vertical(g38)
    c: Coincident(g39,g38)
    c: Coincident(g39,g29)
    c: Horizontal(g39)
    c: Coincident(g40,g35)
    c: Coincident(g40,g35)
    c: Vertical(g37)
    c: Tangent(g36,g29) = 1.5708
    c: Tangent(g44,g36) = -1.5708
    c: Tangent(g44,g37) = -1.5708
    c: Tangent(g43,g38) = -1.5708
    c: Tangent(g43,g34) = -1.5708
    c: Tangent(g34,g30) = 1.5708
    c: Tangent(g33,g30) = -1.5708
    c: Tangent(g42,g33) = 1.5708
    c: Angle(g34,g38) = -0.785398
    c: Parallel(g33,g34)
    c: Equal(g30,g29)
    c: Radius(g30) = 4
    c: Equal(g35,g28)
    c: Horizontal(g36)
    c: Equal(g44,g42)
    c: Equal(g42,g43)
    c: Radius(g42) = 2
    c: Tangent(g41,g37) = -1.5708
    c: Horizontal(g45)
    c: Horizontal(g46)
    c: Tangent(g47,g42) = -1.5708
    c: Horizontal(g47)
    c: Tangent(g45,g41) = -1.5708
    c: Vertical(g54)
    c: Tangent(g48,g45) = -1.5708
    c: Tangent(g55,g48) = 1.5708
    c: Tangent(g55,g31) = -1.5708
    c: Tangent(g54,g31) = -1.5708
    c: Tangent(g54,g49) = 1.5708
    c: Tangent(g49,g46) = -1.5708
    c: Tangent(g50,g46) = -1.5708
    c: Tangent(g53,g50) = 1.5708
    c: Tangent(g53,g32) = -1.5708
    c: Tangent(g52,g32) = 1.5708
    c: Tangent(g52,g51) = -1.5708
    c: Tangent(g51,g47) = -1.5708
    c: Vertical(g52)
    c: Vertical(g53)
    c: Vertical(g55)
    c: Equal(g42,g51)
    c: Equal(g51,g50)
    c: Equal(g50,g49)
    c: Equal(g49,g48)
    c: Equal(g32,g49)
    c: Equal(g0,g7)
    c: Diameter(g0) = 4
FEATURE [TechDraw::DrawSVGTemplate] Template
  EditableTexts = approval_person=B. Hecate; creator=Jon Sagebrand; date_of_issue=2026-02-22; document_type=Component Drawing; general_tolerances=ISO 2768-m; identification_number=DN; language_code=EN; legal_owner_1=Jonix; part_material=Stainless steel Mat.No. 1.4301; revision_index=AAA; scale=1 : 1; sheet_number=1 / 1; title=Makita LXT 18V - Battery Adapter v3
  Height = 210
  Orientation = 1
  Template = <path>
  Width = 297
FEATURE [TechDraw::DrawProjGroupItem] View  label="Single Bottom001"
  CoarseView = false
  Direction = (0,0,1)
  Focus = 100
  HardHidden = false
  IsoCount = 0
  IsoHidden = false
  IsoVisible = false
  LockPosition = false
  Perspective = false
  Rotation = 0
  RotationVector = (1,0,0)
  ScaleType = 0
  ScrubCount = 1
  SeamHidden = false
  SeamVisible = false
  SmoothHidden = false
  SmoothVisible = true
  Source = -> [Pocket010]
  Type = 0
  X = 231.232
  XDirection = (1,0,0)
  Y = 115.403
FEATURE [TechDraw::DrawViewDimension] Dimension
  AngleOverride = false
  Arbitrary = false
  ArbitraryTolerances = false
  BoxCorners = (2) [(-45.4503,-36,0),(45.4503,36,0)]
  EqualTolerance = true
  ExtensionAngle = 0
  FormatSpec = %.2w
  FormatSpecOverTolerance = %+.2w
  FormatSpecUnderTolerance = %+.2w
  Inverted = false
  LineAngle = 0
  LockPosition = false
  MeasureType = 1
  OverTolerance = 0
  References2D = -> [View]
  Rotation = 0
  ScaleType = 0
  TheoreticalExact = false
  Type = 2
  UnderTolerance = 0
  X = -62.2725
  Y = 11.95
FEATURE [TechDraw::DrawViewDimension] Dimension001
  AngleOverride = false
  Arbitrary = false
  ArbitraryTolerances = false
  BoxCorners = (2) [(-45.4503,-36,0),(45.4503,36,0)]
  EqualTolerance = true
  ExtensionAngle = 0
  FormatSpec = %.2w
  FormatSpecOverTolerance = %+.2w
  FormatSpecUnderTolerance = %+.2w
  Inverted = false
  LineAngle = 0
  LockPosition = false
  MeasureType = 1
  OverTolerance = 0
  References2D = -> [View]
  Rotation = 0
  ScaleType = 0
  TheoreticalExact = false
  Type = 2
  UnderTolerance = 0
  X = -74.16
  Y = 0
FEATURE [TechDraw::DrawViewDimension] Dimension002
  AngleOverride = false
  Arbitrary = false
  ArbitraryTolerances = false
  BoxCorners = (2) [(-45.4503,-36,0),(45.4503,36,0)]
  EqualTolerance = true
  ExtensionAngle = 0
  FormatSpec = %.2w
  FormatSpecOverTolerance = %+.2w
  FormatSpecUnderTolerance = %+.2w
  Inverted = false
  LineAngle = 0
  LockPosition = false
  MeasureType = 1
  OverTolerance = 0
  References2D = -> [View]
  Rotation = 0
  ScaleType = 0
  TheoreticalExact = false
  Type = 1
  UnderTolerance = 0
  X = -15.9646
  Y = 82.2651
FEATURE [TechDraw::DrawViewDimension] Dimension003
  AngleOverride = false
  Arbitrary = false
  ArbitraryTolerances = false
  BoxCorners = (2) [(-45.4503,-36,0),(45.4503,36,0)]
  EqualTolerance = true
  ExtensionAngle = 0
  FormatSpec = %.2w
  FormatSpecOverTolerance = %+.2w
  FormatSpecUnderTolerance = %+.2w
  Inverted = false
  LineAngle = 0
  LockPosition = false
  MeasureType = 1
  OverTolerance = 0
  References2D = -> [View]
  Rotation = 0
  ScaleType = 0
  TheoreticalExact = false
  Type = 1
  UnderTolerance = 0
  X = 0.578396
  Y = 73.3427
FEATURE [TechDraw::DrawViewDimension] Dimension004
  AngleOverride = false
  Arbitrary = false
  ArbitraryTolerances = false
  BoxCorners = (2) [(-45.4503,-36,0),(45.4503,36,0)]
  EqualTolerance = true
  ExtensionAngle = 0
  FormatSpec = %.2w
  FormatSpecOverTolerance = %+.2w
  FormatSpecUnderTolerance = %+.2w
  Inverted = false
  LineAngle = 0
  LockPosition = false
  MeasureType = 1
  OverTolerance = 0
  References2D = -> [View]
  Rotation = 0
  ScaleType = 0
  TheoreticalExact = false
  Type = 2
  UnderTolerance = 0
  X = -67.16
  Y = 51.677
FEATURE [TechDraw::DrawProjGroupItem] View001  label="Holder001"
  CoarseView = false
  Direction = (0,0,1)
  Focus = 100
  HardHidden = false
  IsoCount = 0
  IsoHidden = false
  IsoVisible = false
  LockPosition = false
  Perspective = false
  Rotation = 0
  RotationVector = (1,0,0)
  ScaleType = 0
  ScrubCount = 1
  SeamHidden = false
  SeamVisible = false
  SmoothHidden = false
  SmoothVisible = true
  Source = -> [Body001]
  Type = 0
  X = 106.639
  XDirection = (1,0,0)
  Y = 115.403
FEATURE [TechDraw::DrawViewDimension] Dimension005
  AngleOverride = false
  Arbitrary = false
  ArbitraryTolerances = false
  BoxCorners = (2) [(-45.4503,-36,-1e-07),(45.4503,36,1e-07)]
  EqualTolerance = true
  ExtensionAngle = 0
  FormatSpec = %.2w
  FormatSpecOverTolerance = %+.2w
  FormatSpecUnderTolerance = %+.2w
  Inverted = false
  LineAngle = 0
  LockPosition = false
  MeasureType = 1
  OverTolerance = 0
  References2D = -> [View001]
  Rotation = 0
  ScaleType = 0
  TheoreticalExact = false
  Type = 2
  UnderTolerance = 0
  X = -59.9592
  Y = 15.0558
FEATURE [TechDraw::DrawViewDimension] Dimension006
  AngleOverride = false
  Arbitrary = false
  ArbitraryTolerances = false
  BoxCorners = (2) [(-45.4503,-36,-1e-07),(45.4503,36,1e-07)]
  EqualTolerance = true
  ExtensionAngle = 0
  FormatSpec = %.2w
  FormatSpecOverTolerance = %+.2w
  FormatSpecUnderTolerance = %+.2w
  Inverted = false
  LineAngle = 0
  LockPosition = false
  MeasureType = 1
  OverTolerance = 0
  References2D = -> [View001]
  Rotation = 0
  ScaleType = 0
  TheoreticalExact = false
  Type = 2
  UnderTolerance = 0
  X = -73.2672
  Y = 6.8089
FEATURE [TechDraw::DrawViewDimension] Dimension007
  AngleOverride = false
  Arbitrary = false
  ArbitraryTolerances = false
  BoxCorners = (2) [(-45.4503,-36,-1e-07),(45.4503,36,1e-07)]
  EqualTolerance = true
  ExtensionAngle = 0
  FormatSpec = %.2w
  FormatSpecOverTolerance = %+.2w
  FormatSpecUnderTolerance = %+.2w
  Inverted = false
  LineAngle = 0
  LockPosition = false
  MeasureType = 1
  OverTolerance = 0
  References2D = -> [View001]
  Rotation = 0
  ScaleType = 0
  TheoreticalExact = false
  Type = 2
  UnderTolerance = 0
  X = -66.2672
  Y = 45.718
FEATURE [TechDraw::DrawViewDimension] Dimension008
  AngleOverride = false
  Arbitrary = false
  ArbitraryTolerances = false
  BoxCorners = (2) [(-45.4503,-36,-1e-07),(45.4503,36,1e-07)]
  EqualTolerance = true
  ExtensionAngle = 0
  FormatSpec = %.2w
  FormatSpecOverTolerance = %+.2w
  FormatSpecUnderTolerance = %+.2w
  Inverted = false
  LineAngle = 0
  LockPosition = false
  MeasureType = 1
  OverTolerance = 0
  References2D = -> [View001]
  Rotation = 0
  ScaleType = 0
  TheoreticalExact = false
  Type = 1
  UnderTolerance = 0
  X = -24.4221
  Y = 64.3637
FEATURE [TechDraw::DrawViewDimension] Dimension009
  AngleOverride = false
  Arbitrary = false
  ArbitraryTolerances = false
  BoxCorners = (2) [(-45.4503,-36,-1e-07),(45.4503,36,1e-07)]
  EqualTolerance = true
  ExtensionAngle = 0
  FormatSpec = %.2w
  FormatSpecOverTolerance = %+.2w
  FormatSpecUnderTolerance = %+.2w
  Inverted = false
  LineAngle = 0
  LockPosition = false
  MeasureType = 1
  OverTolerance = 0
  References2D = -> [View001]
  Rotation = 0
  ScaleType = 0
  TheoreticalExact = false
  Type = 1
  UnderTolerance = 0
  X = -2.26279
  Y = 53.1648
FEATURE [TechDraw::DrawViewDimension] Dimension011
  AngleOverride = false
  Arbitrary = false
  ArbitraryTolerances = false
  BoxCorners = (2) [(-45.4503,-36,0),(45.4503,36,0)]
  EqualTolerance = true
  ExtensionAngle = 0
  FormatSpec = R%.2w
  FormatSpecOverTolerance = %+.2w
  FormatSpecUnderTolerance = %+.2w
  Inverted = false
  LineAngle = 0
  LockPosition = false
  MeasureType = 1
  OverTolerance = 0
  References2D = -> [View]
  Rotation = 0
  ScaleType = 0
  TheoreticalExact = false
  Type = 4
  UnderTolerance = 0
  X = -27.7134
  Y = 18.1571
FEATURE [TechDraw::DrawViewDimension] Dimension012
  AngleOverride = false
  Arbitrary = false
  ArbitraryTolerances = false
  BoxCorners = (2) [(-45.4503,-36,0),(45.4503,36,0)]
  EqualTolerance = true
  ExtensionAngle = 0
  FormatSpec = R%.2w
  FormatSpecOverTolerance = %+.2w
  FormatSpecUnderTolerance = %+.2w
  Inverted = false
  LineAngle = 0
  LockPosition = false
  MeasureType = 1
  OverTolerance = 0
  References2D = -> [View]
  Rotation = 0
  ScaleType = 0
  TheoreticalExact = false
  Type = 4
  UnderTolerance = 0
  X = -16.0069
  Y = 2.03072
FEATURE [TechDraw::DrawViewDimension] Dimension013
  AngleOverride = false
  Arbitrary = false
  ArbitraryTolerances = false
  BoxCorners = (2) [(-45.4503,-36,0),(45.4503,36,0)]
  EqualTolerance = true
  ExtensionAngle = 0
  FormatSpec = R%.2w
  FormatSpecOverTolerance = %+.2w
  FormatSpecUnderTolerance = %+.2w
  Inverted = false
  LineAngle = 0
  LockPosition = false
  MeasureType = 1
  OverTolerance = 0
  References2D = -> [View]
  Rotation = 0
  ScaleType = 0
  TheoreticalExact = false
  Type = 4
  UnderTolerance = 0
  X = -2.8669
  Y = 30.3414
FEATURE [TechDraw::DrawViewDimension] Dimension014
  AngleOverride = false
  Arbitrary = false
  ArbitraryTolerances = false
  BoxCorners = (2) [(-45.4503,-36,0),(45.4503,36,0)]
  EqualTolerance = true
  ExtensionAngle = 0
  FormatSpec = %.2w
  FormatSpecOverTolerance = %+.2w
  FormatSpecUnderTolerance = %+.2w
  Inverted = false
  LineAngle = 0
  LockPosition = false
  MeasureType = 1
  OverTolerance = 0
  References2D = -> [View]
  Rotation = 0
  ScaleType = 0
  TheoreticalExact = false
  Type = 1
  UnderTolerance = 0
  X = 23.3541
  Y = 18.2756
FEATURE [TechDraw::DrawViewDimension] Dimension015
  AngleOverride = false
  Arbitrary = false
  ArbitraryTolerances = false
  BoxCorners = (2) [(-45.4503,-36,0),(45.4503,36,0)]
  EqualTolerance = true
  ExtensionAngle = 0
  FormatSpec = %.2w
  FormatSpecOverTolerance = %+.2w
  FormatSpecUnderTolerance = %+.2w
  Inverted = false
  LineAngle = 0
  LockPosition = false
  MeasureType = 1
  OverTolerance = 0
  References2D = -> [View]
  Rotation = 0
  ScaleType = 0
  TheoreticalExact = false
  Type = 1
  UnderTolerance = 0
  X = 9.7261
  Y = 13.0674
FEATURE [TechDraw::DrawViewDimension] Dimension016
  AngleOverride = false
  Arbitrary = false
  ArbitraryTolerances = false
  BoxCorners = (2) [(-45.4503,-36,0),(45.4503,36,0)]
  EqualTolerance = true
  ExtensionAngle = 0
  FormatSpec = %.2w
  FormatSpecOverTolerance = %+.2w
  FormatSpecUnderTolerance = %+.2w
  Inverted = false
  LineAngle = 0
  LockPosition = false
  MeasureType = 1
  OverTolerance = 0
  References2D = -> [View]
  Rotation = 0
  ScaleType = 0
  TheoreticalExact = false
  Type = 2
  UnderTolerance = 0
  X = 5.41211
  Y = -7.76453
FEATURE [TechDraw::DrawViewDimension] Dimension017
  AngleOverride = false
  Arbitrary = false
  ArbitraryTolerances = false
  BoxCorners = (2) [(-45.4503,-36,0),(45.4503,36,0)]
  EqualTolerance = true
  ExtensionAngle = 0
  FormatSpec = %.2w
  FormatSpecOverTolerance = %+.2w
  FormatSpecUnderTolerance = %+.2w
  Inverted = false
  LineAngle = 0
  LockPosition = false
  MeasureType = 1
  OverTolerance = 0
  References2D = -> [View]
  Rotation = 0
  ScaleType = 0
  TheoreticalExact = false
  Type = 1
  UnderTolerance = 0
  X = 2.1628
  Y = 54.0917
FEATURE [TechDraw::DrawViewDimension] Dimension018
  AngleOverride = false
  Arbitrary = false
  ArbitraryTolerances = false
  BoxCorners = (2) [(-45.4503,-36,0),(45.4503,36,0)]
  EqualTolerance = true
  ExtensionAngle = 0
  FormatSpec = %.2w
  FormatSpecOverTolerance = %+.2w
  FormatSpecUnderTolerance = %+.2w
  Inverted = false
  LineAngle = 0
  LockPosition = false
  MeasureType = 1
  OverTolerance = 0
  References2D = -> [View]
  Rotation = 0
  ScaleType = 0
  TheoreticalExact = false
  Type = 2
  UnderTolerance = 0
  X = -7.43235
  Y = 0
FEATURE [TechDraw::DrawViewDimension] Dimension019
  AngleOverride = false
  Arbitrary = false
  ArbitraryTolerances = false
  BoxCorners = (2) [(-45.4503,-36,0),(45.4503,36,0)]
  EqualTolerance = true
  ExtensionAngle = 0
  FormatSpec = %.2w
  FormatSpecOverTolerance = %+.2w
  FormatSpecUnderTolerance = %+.2w
  Inverted = false
  LineAngle = 0
  LockPosition = false
  MeasureType = 1
  OverTolerance = 0
  References2D = -> [View]
  Rotation = 0
  ScaleType = 0
  TheoreticalExact = false
  Type = 1
  UnderTolerance = 0
  X = 1.30741
  Y = 63.3671
FEATURE [TechDraw::DrawPage] Page  label="Holder and Single Bottom Top"
  KeepUpdated = true
  NextBalloonIndex = 1
  ProjectionType = 0
  Template = -> Template
  Views = -> [View,Dimension,Dimension001,Dimension002,Dimension003,Dimension004,View001,Dimension005,Dimension006,Dimension007,Dimension008,Dimension009,Dimension011,Dimension012,Dimension013,Dimension014,Dimension015,Dimension016,Dimension017,Dimension018,Dimension019]
FEATURE [PartDesign::Pocket] Pocket011
  BaseFeature = -> Pad003
  Direction = (0,0,-1)
  Length = 0
  Length2 = 5
  Offset = -2
  Profile = -> Sketch019
  ReferenceAxis = -> Sketch019 [N_Axis]
  Refine = true
  Suppressed = false
  Type = 3
  UpToFace = -> Pad003 [Face7]
FEATURE [Sketcher::SketchObject] Sketch020
  ArcFitTolerance = 1e-06
  AttachmentSupport = -> [Pocket011]
  ExternalGeometry = -> [Pocket011]
  FullyConstrained = true
  MakeInternals = false
  MapMode = 5
  Placement = pos=(0,0,0) rot=(1,0,0;1.5708rad)
  sketch-geometry (4):
    g0: LineSegment StartX=35.66 StartY=-2 StartZ=0 EndX=35.66 EndY=-12 EndZ=0
    g1: LineSegment StartX=35.66 StartY=-12 StartZ=0 EndX=52.86 EndY=-12 EndZ=0
    g2: LineSegment StartX=52.86 StartY=-12 StartZ=0 EndX=52.86 EndY=-2 EndZ=0
    g3: LineSegment StartX=52.86 StartY=-2 StartZ=0 EndX=35.66 EndY=-2 EndZ=0
  constraints (11):
    c: Coincident(g0,g1)
    c: Coincident(g1,g2)
    c: Coincident(g2,g3)
    c: Coincident(g3,g0)
    c: Vertical(g0)
    c: Vertical(g2)
    c: Horizontal(g1)
    c: Horizontal(g3)
    c: PointOnObject(g0,g-3)
    c: Coincident(g1,g-4)
    c: DistanceY(g0,g-3) = 2
FEATURE [PartDesign::Pocket] Pocket012
  BaseFeature = -> Pocket011
  Direction = (0,1,-2e-16)
  Length = 5
  Length2 = 5
  Profile = -> Sketch020
  ReferenceAxis = -> Sketch020 [N_Axis]
  Refine = true
  Suppressed = false
  Type = 2
FEATURE [TechDraw::DrawSVGTemplate] Template001
  EditableTexts = approval_person=B. Hecate; creator=Jon Sagebrand; date_of_issue=2026-02-22; document_type=Component Drawing; general_tolerances=ISO 2768-m; identification_number=DN; language_code=EN; legal_owner_1=Jonix; part_material=Stainless steel Mat.No. 1.4301; revision_index=AAA; scale=1 : 1; sheet_number=2 / 2; title=Makita LXT 18V - Battery Adapter v3
  Height = 210
  Orientation = 1
  Template = <path>
  Width = 297
FEATURE [TechDraw::DrawProjGroupItem] View002  label="Bottom USB Outlet"
  CoarseView = false
  Direction = (0,-1,0)
  Focus = 100
  HardHidden = false
  IsoCount = 0
  IsoHidden = false
  IsoVisible = false
  LockPosition = false
  Perspective = false
  Rotation = 0
  RotationVector = (1,0,0)
  ScaleType = 0
  ScrubCount = 1
  SeamHidden = false
  SeamVisible = false
  SmoothHidden = false
  SmoothVisible = true
  Source = -> [Body002]
  Type = 0
  X = 214.01
  XDirection = (1,0,0)
  Y = 122.584
FEATURE [TechDraw::DrawViewDimension] Dimension020
  AngleOverride = false
  Arbitrary = false
  ArbitraryTolerances = false
  BoxCorners = (2) [(-45.4503,-8.25,-1e-07),(45.4503,8.25,1e-07)]
  EqualTolerance = true
  ExtensionAngle = 0
  FormatSpec = %.2w
  FormatSpecOverTolerance = %+.2w
  FormatSpecUnderTolerance = %+.2w
  Inverted = false
  LineAngle = 0
  LockPosition = false
  MeasureType = 1
  OverTolerance = 0
  References2D = -> [View002]
  Rotation = 0
  ScaleType = 0
  TheoreticalExact = false
  Type = 2
  UnderTolerance = 0
  X = -71.1009
  Y = 9.37462
FEATURE [TechDraw::DrawViewDimension] Dimension021
  AngleOverride = false
  Arbitrary = false
  ArbitraryTolerances = false
  BoxCorners = (2) [(-45.4503,-8.25,-1e-07),(45.4503,8.25,1e-07)]
  EqualTolerance = true
  ExtensionAngle = 0
  FormatSpec = %.2w
  FormatSpecOverTolerance = %+.2w
  FormatSpecUnderTolerance = %+.2w
  Inverted = false
  LineAngle = 0
  LockPosition = false
  MeasureType = 1
  OverTolerance = 0
  References2D = -> [View002]
  Rotation = 0
  ScaleType = 0
  TheoreticalExact = false
  Type = 2
  UnderTolerance = 0
  X = -26.4866
  Y = 24.4881
FEATURE [TechDraw::DrawViewDimension] Dimension022
  AngleOverride = false
  Arbitrary = false
  ArbitraryTolerances = false
  BoxCorners = (2) [(-45.4503,-8.25,-1e-07),(45.4503,8.25,1e-07)]
  EqualTolerance = true
  ExtensionAngle = 0
  FormatSpec = %.2w
  FormatSpecOverTolerance = %+.2w
  FormatSpecUnderTolerance = %+.2w
  Inverted = false
  LineAngle = 0
  LockPosition = false
  MeasureType = 1
  OverTolerance = 0
  References2D = -> [View002]
  Rotation = 0
  ScaleType = 0
  TheoreticalExact = false
  Type = 2
  UnderTolerance = 0
  X = -64.1009
  Y = 17.4216
FEATURE [TechDraw::DrawViewDimension] Dimension023
  AngleOverride = false
  Arbitrary = false
  ArbitraryTolerances = false
  BoxCorners = (2) [(-45.4503,-8.25,-1e-07),(45.4503,8.25,1e-07)]
  EqualTolerance = true
  ExtensionAngle = 0
  FormatSpec = %.2w
  FormatSpecOverTolerance = %+.2w
  FormatSpecUnderTolerance = %+.2w
  Inverted = false
  LineAngle = 0
  LockPosition = false
  MeasureType = 1
  OverTolerance = 0
  References2D = -> [View002]
  Rotation = 0
  ScaleType = 0
  TheoreticalExact = false
  Type = 1
  UnderTolerance = 0
  X = 29.9718
  Y = 31.669
FEATURE [TechDraw::DrawProjGroupItem] View003  label="Bottom 18V Outlet"
  CoarseView = false
  Direction = (1,-1e-16,0)
  Focus = 100
  HardHidden = false
  IsoCount = 0
  IsoHidden = false
  IsoVisible = false
  LockPosition = false
  Perspective = false
  Rotation = 0
  RotationVector = (1,0,0)
  ScaleType = 0
  ScrubCount = 1
  SeamHidden = false
  SeamVisible = false
  SmoothHidden = false
  SmoothVisible = true
  Source = -> [Body002]
  Type = 0
  X = 88.39
  XDirection = (1e-16,1,0)
  Y = 122.584
FEATURE [TechDraw::DrawViewDimension] Dimension024
  AngleOverride = false
  Arbitrary = false
  ArbitraryTolerances = false
  BoxCorners = (2) [(-36,-8.25,-1e-07),(36,8.25,1e-07)]
  EqualTolerance = true
  ExtensionAngle = 0
  FormatSpec = %.2w
  FormatSpecOverTolerance = %+.2w
  FormatSpecUnderTolerance = %+.2w
  Inverted = false
  LineAngle = 0
  LockPosition = false
  MeasureType = 1
  OverTolerance = 0
  References2D = -> [View003]
  Rotation = 0
  ScaleType = 0
  TheoreticalExact = false
  Type = 2
  UnderTolerance = 0
  X = -49.3965
  Y = 20.7306
FEATURE [TechDraw::DrawViewDimension] Dimension025
  AngleOverride = false
  Arbitrary = false
  ArbitraryTolerances = false
  BoxCorners = (2) [(-36,-8.25,-1e-07),(36,8.25,1e-07)]
  EqualTolerance = true
  ExtensionAngle = 0
  FormatSpec = %.2w
  FormatSpecOverTolerance = %+.2w
  FormatSpecUnderTolerance = %+.2w
  Inverted = false
  LineAngle = 0
  LockPosition = false
  MeasureType = 1
  OverTolerance = 0
  References2D = -> [View003]
  Rotation = 0
  ScaleType = 0
  TheoreticalExact = false
  Type = 1
  UnderTolerance = 0
  X = 0
  Y = 25.7363
FEATURE [TechDraw::DrawViewDimension] Dimension026
  AngleOverride = false
  Arbitrary = false
  ArbitraryTolerances = false
  BoxCorners = (2) [(-36,-8.25,-1e-07),(36,8.25,1e-07)]
  EqualTolerance = true
  ExtensionAngle = 0
  FormatSpec = %.2w
  FormatSpecOverTolerance = %+.2w
  FormatSpecUnderTolerance = %+.2w
  Inverted = false
  LineAngle = 0
  LockPosition = false
  MeasureType = 1
  OverTolerance = 0
  References2D = -> [View003]
  Rotation = 0
  ScaleType = 0
  TheoreticalExact = false
  Type = 2
  UnderTolerance = 0
  X = -46.6386
  Y = -14.467
FEATURE [TechDraw::DrawPage] Page001  label="SIngle Botom Outlets"
  KeepUpdated = true
  NextBalloonIndex = 1
  ProjectionType = 0
  Template = -> Template001
  Views = -> [View002,Dimension020,Dimension021,Dimension022,Dimension023,View003,Dimension024,Dimension025,Dimension026]
FEATURE [Sketcher::SketchObject] Sketch021
  ArcFitTolerance = 1e-06
  AttachmentSupport = -> [Pocket012]
  ExternalGeometry = -> [Pocket012]
  FullyConstrained = true
  MakeInternals = false
  MapMode = 5
  Placement = pos=(87.55,0,0) rot=(0.57735,0.57735,0.57735;2.0944rad)
  sketch-geometry (4):
    g0: LineSegment StartX=8.5 StartY=-12 StartZ=0 EndX=8.5 EndY=-3 EndZ=0
    g1: LineSegment StartX=8.5 StartY=-3 StartZ=0 EndX=0 EndY=-3 EndZ=0
    g2: LineSegment StartX=0 StartY=-3 StartZ=0 EndX=0 EndY=-12 EndZ=0
    g3: LineSegment StartX=0 StartY=-12 StartZ=0 EndX=8.5 EndY=-12 EndZ=0
  constraints (12):
    c: Coincident(g0,g1)
    c: Coincident(g1,g2)
    c: Coincident(g2,g3)
    c: Coincident(g3,g0)
    c: Vertical(g0)
    c: Vertical(g2)
    c: Horizontal(g1)
    c: Horizontal(g3)
    c: PointOnObject(g0,g-3)
    c: PointOnObject(g1,g-2)
    c: DistanceY(g0,g0) = 9
    c: DistanceX(g1,g1) = 8.5
FEATURE [PartDesign::Pocket] Pocket013
  BaseFeature = -> Pocket012
  Direction = (-1,0,0)
  Length = 0
  Length2 = 5
  Profile = -> Sketch021
  ReferenceAxis = -> Sketch021 [N_Axis]
  Refine = true
  Suppressed = false
  Type = 3
  UpToFace = -> Pocket012 [Face14]
FEATURE [Sketcher::SketchObject] Sketch023
  ArcFitTolerance = 1e-06
  AttachmentSupport = -> [Pocket013]
  FullyConstrained = true
  MakeInternals = false
  MapMode = 5
  Placement = pos=(0,0,-12) rot=(0,0,1;0rad)
  sketch-geometry (9):
    g0: LineSegment StartX=65.55 StartY=0 StartZ=0 EndX=71.55 EndY=0 EndZ=0
    g1: LineSegment StartX=71.55 StartY=0 StartZ=0 EndX=71.55 EndY=1 EndZ=0
    g2: LineSegment StartX=71.55 StartY=1 StartZ=0 EndX=65.55 EndY=1 EndZ=0
    g3: LineSegment StartX=65.55 StartY=1 StartZ=0 EndX=65.55 EndY=0 EndZ=0
    g4: LineSegment StartX=65.55 StartY=39.5 StartZ=0 EndX=65.55 EndY=37.5 EndZ=0
    g5: LineSegment StartX=65.55 StartY=37.5 StartZ=0 EndX=71.55 EndY=37.5 EndZ=0
    g6: LineSegment StartX=71.55 StartY=37.5 StartZ=0 EndX=71.55 EndY=39.5 EndZ=0
    g7: LineSegment StartX=71.55 StartY=39.5 StartZ=0 EndX=65.55 EndY=39.5 EndZ=0
    g8: GeomPoint [constr] X=68.55 Y=38.5 Z=0
  constraints (25):
    c: Coincident(g0,g1)
    c: Coincident(g1,g2)
    c: Coincident(g2,g3)
    c: Coincident(g3,g0)
    c: Horizontal(g0)
    c: Horizontal(g2)
    c: Vertical(g1)
    c: Vertical(g3)
    c: PointOnObject(g0,g-1)
    c: Coincident(g4,g5)
    c: Coincident(g5,g6)
    c: Coincident(g6,g7)
    c: Coincident(g7,g4)
    c: Vertical(g4)
    c: Vertical(g6)
    c: Horizontal(g5)
    c: Horizontal(g7)
    c: Symmetric(g6,g4,g8)
    c: Horizontal(g8,g-3)
    c: Equal(g2,g5)
    c: Vertical(g5,g1)
    c: DistanceX(g6,g-4) = 16
    c: DistanceX(g2,g2) = 6
    c: DistanceY(g4,g4) = 2
    c: DistanceY(g1,g1) = 1
FEATURE [PartDesign::Pad] Pad004
  BaseFeature = -> Pocket013
  Direction = (0,0,1)
  Length = 10
  Length2 = 10
  Profile = -> Sketch023
  ReferenceAxis = -> Sketch023 [N_Axis]
  Refine = true
  Suppressed = false
  Type = 3
  UpToFace = -> Pocket013 [Face4]
FEATURE [Sketcher::SketchObject] Sketch024
  ArcFitTolerance = 1e-06
  AttachmentSupport = -> [Pad004]
  ExternalGeometry = -> [Pad004]
  FullyConstrained = true
  MakeInternals = false
  MapMode = 5
  Placement = pos=(0,37.5,0) rot=(1,0,0;1.5708rad)
  sketch-geometry (5):
    g0: LineSegment StartX=71.55 StartY=0 StartZ=0 EndX=71.55 EndY=-4 EndZ=0
    g1: LineSegment StartX=71.55 StartY=-4 StartZ=0 EndX=69.55 EndY=-4 EndZ=0
    g2: LineSegment StartX=69.55 StartY=-4 StartZ=0 EndX=65.55 EndY=-8 EndZ=0
    g3: LineSegment StartX=65.55 StartY=-8 StartZ=0 EndX=65.55 EndY=0 EndZ=0
    g4: LineSegment StartX=65.55 StartY=0 StartZ=0 EndX=71.55 EndY=0 EndZ=0
  constraints (13):
    c: Coincident(g-3,g0)
    c: PointOnObject(g0,g-3)
    c: Coincident(g0,g1)
    c: Horizontal(g1)
    c: Coincident(g1,g2)
    c: PointOnObject(g2,g-4)
    c: Coincident(g2,g3)
    c: Coincident(g3,g-4)
    c: Coincident(g3,g4)
    c: Coincident(g4,g0)
    c: DistanceY(g-3,g0) = 8
    c: DistanceX(g1,g1) = 2
    c: Angle(g2,g3) = 0.785398
FEATURE [PartDesign::Pocket] Pocket015
  BaseFeature = -> Pad004
  Direction = (0,1,-2e-16)
  Length = 5
  Length2 = 5
  Profile = -> Sketch024
  ReferenceAxis = -> Sketch024 [N_Axis]
  Refine = true
  Suppressed = false
  Type = 2
FEATURE [Sketcher::SketchObject] Sketch025
  ArcFitTolerance = 1e-06
  AttachmentSupport = -> [Pocket015]
  ExternalGeometry = -> [Pocket015]
  FullyConstrained = true
  MakeInternals = false
  MapMode = 5
  sketch-geometry (4):
    g0: Circle CenterX=56.86 CenterY=20.5 CenterZ=0 NormalX=0 NormalY=0 NormalZ=1 AngleXU=0 Radius=2
    g1: Circle CenterX=31.66 CenterY=20.5 CenterZ=0 NormalX=0 NormalY=0 NormalZ=1 AngleXU=0 Radius=2
    g2: Circle CenterX=56.86 CenterY=56.5 CenterZ=0 NormalX=0 NormalY=0 NormalZ=1 AngleXU=0 Radius=2
    g3: Circle CenterX=31.66 CenterY=56.5 CenterZ=0 NormalX=0 NormalY=0 NormalZ=1 AngleXU=0 Radius=2
  constraints (8):
    c: Coincident(g0,g-6)
    c: Coincident(g1,g-5)
    c: Coincident(g2,g-3)
    c: Coincident(g3,g-4)
    c: Equal(g2,g3)
    c: Equal(g3,g1)
    c: Equal(g1,g0)
    c: Equal(g0,g-6)
FEATURE [PartDesign::Pad] Pad005
  BaseFeature = -> Pocket015
  Direction = (0,0,1)
  Length = 2.5
  Length2 = 10
  Profile = -> Sketch025
  ReferenceAxis = -> Sketch025 [N_Axis]
  Refine = true
  Suppressed = false
  Type = 0
FEATURE [PartDesign::Mirrored] Mirrored002  label="Pad006"
  BaseFeature = -> Pad005
  MirrorPlane = -> XZ_Plane007
  Originals = -> [Pad005]
  Refine = true
  Suppressed = false
  TransformMode = 1
FEATURE [Sketcher::SketchObject] Sketch026
  ArcFitTolerance = 1e-06
  AttachmentSupport = -> [Mirrored002]
  ExternalGeometry = -> [Mirrored002]
  FullyConstrained = true
  MakeInternals = false
  MapMode = 5
  Placement = pos=(0,9e-16,-4) rot=(0,0,1;0rad)
  sketch-geometry (4):
    g0: LineSegment StartX=65.55 StartY=-37.5 StartZ=0 EndX=65.55 EndY=-39.5 EndZ=0
    g1: LineSegment StartX=65.55 StartY=-39.5 StartZ=0 EndX=71.55 EndY=-39.5 EndZ=0
    g2: LineSegment StartX=71.55 StartY=-39.5 StartZ=0 EndX=71.55 EndY=-37.5 EndZ=0
    g3: LineSegment StartX=71.55 StartY=-37.5 StartZ=0 EndX=65.55 EndY=-37.5 EndZ=0
  constraints (10):
    c: Coincident(g0,g1)
    c: Coincident(g1,g2)
    c: Coincident(g2,g3)
    c: Coincident(g3,g0)
    c: Vertical(g0)
    c: Vertical(g2)
    c: Horizontal(g1)
    c: Horizontal(g3)
    c: Coincident(g0,g-3)
    c: Coincident(g1,g-4)
FEATURE [PartDesign::Pocket] Pocket016  label="36V Outlet"
  BaseFeature = -> Mirrored002
  Direction = (0,0,-1)
  Length = 0
  Length2 = 5
  Profile = -> Sketch026
  ReferenceAxis = -> Sketch026 [N_Axis]
  Refine = true
  Suppressed = false
  Type = 3
  UpToFace = -> Mirrored002 [Face132]
FEATURE [Sketcher::SketchObject] Sketch027
  ArcFitTolerance = 1e-06
  AttachmentSupport = -> [Pocket016]
  ExternalGeometry = -> [Pocket016]
  FullyConstrained = true
  MakeInternals = false
  MapMode = 5
  Placement = pos=(87.55,0,0) rot=(0.57735,0.57735,0.57735;2.0944rad)
  sketch-geometry (5):
    g0: LineSegment StartX=30 StartY=-3 StartZ=0 EndX=30 EndY=-12 EndZ=0
    g1: LineSegment StartX=30 StartY=-12 StartZ=0 EndX=47 EndY=-12 EndZ=0
    g2: LineSegment StartX=47 StartY=-12 StartZ=0 EndX=47 EndY=-3 EndZ=0
    g3: LineSegment StartX=47 StartY=-3 StartZ=0 EndX=30 EndY=-3 EndZ=0
    g4: GeomPoint [constr] X=38.5 Y=-7.5 Z=0
  constraints (13):
    c: Coincident(g0,g1)
    c: Coincident(g1,g2)
    c: Coincident(g2,g3)
    c: Coincident(g3,g0)
    c: Vertical(g0)
    c: Vertical(g2)
    c: Horizontal(g1)
    c: Horizontal(g3)
    c: Symmetric(g2,g0,g4)
    c: Vertical(g4,g-4)
    c: Horizontal(g0,g-6)
    c: Equal(g0,g-6)
    c: Equal(g3,g-5)
FEATURE [PartDesign::Pocket] Pocket017  label="18V + 36V Outlets"
  BaseFeature = -> Pocket016
  Direction = (-1,0,0)
  Length = 5
  Length2 = 5
  Profile = -> Sketch027
  ReferenceAxis = -> Sketch027 [N_Axis]
  Refine = true
  Suppressed = false
  Type = 2
FEATURE [Sketcher::SketchObject] Sketch028
  ArcFitTolerance = 1e-06
  AttachmentSupport = -> [Pocket017]
  ExternalGeometry = -> [Pocket017]
  FullyConstrained = true
  MakeInternals = false
  MapMode = 5
  Placement = pos=(87.55,0,0) rot=(0.57735,0.57735,0.57735;2.0944rad)
  sketch-geometry (5):
    g0: LineSegment StartX=-45.1 StartY=-2.5 StartZ=0 EndX=-45.1 EndY=-8 EndZ=0
    g1: LineSegment StartX=-45.1 StartY=-8 StartZ=0 EndX=-31.9 EndY=-8 EndZ=0
    g2: LineSegment StartX=-31.9 StartY=-8 StartZ=0 EndX=-31.9 EndY=-2.5 EndZ=0
    g3: LineSegment StartX=-31.9 StartY=-2.5 StartZ=0 EndX=-45.1 EndY=-2.5 EndZ=0
    g4: GeomPoint [constr] X=-38.5 Y=-5.25 Z=0
  constraints (13):
    c: Coincident(g0,g1)
    c: Coincident(g1,g2)
    c: Coincident(g2,g3)
    c: Coincident(g3,g0)
    c: Vertical(g0)
    c: Vertical(g2)
    c: Horizontal(g1)
    c: Horizontal(g3)
    c: Symmetric(g2,g0,g4)
    c: Vertical(g-4,g4)
    c: DistanceY(g-4,g0) = 4
    c: DistanceY(g0,g0) = 5.5
    c: DistanceX(g3,g3) = 13.2
FEATURE [PartDesign::Pocket] Pocket018  label="18V + 36V + USB Outlets"
  BaseFeature = -> Pocket017
  Direction = (-1,0,0)
  Length = 5
  Length2 = 5
  Profile = -> Sketch028
  ReferenceAxis = -> Sketch028 [N_Axis]
  Refine = true
  Suppressed = false
  Type = 2
FEATURE [PartDesign::Body] Body003  label="Double Bottom"
  AllowCompound = false
  Group = -> [ShapeBinder001,Sketch018,Pad003,Sketch019,Pocket011,Sketch020,Pocket012,Sketch021,Pocket013,Sketch023,Pad004,Sketch024,Pocket015,Sketch025,Pad005,Mirrored002,Sketch026,Pocket016,Sketch027,Pocket017,Sketch028,Pocket018]
  Origin = -> Origin007
  Tip = -> Pocket018
note: 2 file-system paths scrubbed to <path> (originals preserved in the JSON sidecar)
